# Revit family: Door-Exterior_Interior-Simpson-Sash-Three_Quarter_Glass-Single
name_source: partatom
category: Doors
revit_build: Autodesk Revit Architecture 2012 (Build: 20110916_2132(x64)
units: mm (PartAtom-declared; Revit-internal decimal feet)

## types (483) — shared parameters
Assembly Code = B2030230
Bottom Panel Height = 0' - 11 5/8"
Bottom Rail Height = 0' - 8 11/16"
Construction Type = Wood
Frame = Wood - Simpson Doors - Douglas Fir
Frame Projection Ext. = 0' - 1"
Frame Projection Int. = 0' - 1"
Frame Type = Frame : Standard
Frame Width = 0' - 3"
Function = Exterior
Glass = Glass - Simpson Doors - Clear
Glass Options = http://simpsondoor.com
Innerbond Double Hip-Raised Panel = Yes
Manufacturer = Simpson Door Company
Middle Rail Height = 0' - 6 1/2"
Muntin Width = 0' - 0 1/2"
Ovolo Construction = Yes
Panel = Wood - Simpson Doors - Douglas Fir
Panel Divider Width = 0' - 3 1/2"
Panel Stile Width = 0' - 5"
Product Documentation Link = http://www.simpsondoor.com
Product Page URL = http://www.simpsondoor.com
Thickness = 0' - 1 3/4"
Thickness Note = comes in 1 3/4" and 2 1/4" Thickness. Default is set to 1 3/4"
Top Rail Height = 0' - 3 15/16"
URL = http://www.simpsondoor.com
UltraBlock Note = This Door Comes with The Option of UltraBlock Technology. It is Turn On as a Default
UltraBlock Option = Yes
Wall Closure = By host
WaterBarrier Note = This Door Comes with The Option of WaterBarrier with UltraBlock Technology. It is Turn Off as a Default
WaterBarrier with UltraBlock Technology = No
Wood Species = http://simpsondoor.com
Wood Species Note = Available in Any Wood Species

## per-type parameters (varying)
| type | Description | Height | Model | Number of Horizontal Muntins | Number of Panel Dividers | Number of Vertical Muntins | Rough Height | Rough Width | Width |
| 501 Exterior Sash 30x80 Ovolo Raised Panel | Exterior Sash - Single Lite - Single Panel | 6' - 8" | 501 | 0 | 0 | 0 | 6' - 10" | 2' - 10" | 2' - 6" |
| 501 Exterior Sash 30x84 Ovolo Raised Panel | Exterior Sash - Single Lite - Single Panel | 7' - 0" | 501 | 0 | 0 | 0 | 7' - 2" | 2' - 10" | 2' - 6" |
| 501 Exterior Sash 30x96 Ovolo Raised Panel | Exterior Sash - Single Lite - Single Panel | 8' - 0" | 501 | 0 | 0 | 0 | 8' - 2" | 2' - 10" | 2' - 6" |
| 501 Exterior Sash 32x80 Ovolo Raised Panel | Exterior Sash - Single Lite - Single Panel | 6' - 8" | 501 | 0 | 0 | 0 | 6' - 10" | 3' - 0" | 2' - 8" |
| 501 Exterior Sash 32x84 Ovolo Raised Panel | Exterior Sash - Single Lite - Single Panel | 7' - 0" | 501 | 0 | 0 | 0 | 7' - 2" | 3' - 0" | 2' - 8" |
| 501 Exterior Sash 32x96 Ovolo Raised Panel | Exterior Sash - Single Lite - Single Panel | 8' - 0" | 501 | 0 | 0 | 0 | 8' - 2" | 3' - 0" | 2' - 8" |
| 501 Exterior Sash 34x80 Ovolo Raised Panel | Exterior Sash - Single Lite - Single Panel | 6' - 8" | 501 | 0 | 0 | 0 | 6' - 10" | 3' - 2" | 2' - 10" |
| 501 Exterior Sash 34x84 Ovolo Raised Panel | Exterior Sash - Single Lite - Single Panel | 7' - 0" | 501 | 0 | 0 | 0 | 7' - 2" | 3' - 2" | 2' - 10" |
| 501 Exterior Sash 34x96 Ovolo Raised Panel | Exterior Sash - Single Lite - Single Panel | 8' - 0" | 501 | 0 | 0 | 0 | 8' - 2" | 3' - 2" | 2' - 10" |
| 501 Exterior Sash 36x80 Ovolo Raised Panel | Exterior Sash - Single Lite - Single Panel | 6' - 8" | 501 | 0 | 0 | 0 | 6' - 10" | 3' - 4" | 3' - 0" |
| 501 Exterior Sash 36x84 Ovolo Raised Panel | Exterior Sash - Single Lite - Single Panel | 7' - 0" | 501 | 0 | 0 | 0 | 7' - 2" | 3' - 4" | 3' - 0" |
| 501 Exterior Sash 36x96 Ovolo Raised Panel | Exterior Sash - Single Lite - Single Panel | 8' - 0" | 501 | 0 | 0 | 0 | 8' - 2" | 3' - 4" | 3' - 0" |
| 501 Exterior Sash 38x80 Ovolo Raised Panel | Exterior Sash - Single Lite - Single Panel | 6' - 8" | 501 | 0 | 0 | 0 | 6' - 10" | 3' - 6" | 3' - 2" |
| 501 Exterior Sash 38x84 Ovolo Raised Panel | Exterior Sash - Single Lite - Single Panel | 7' - 0" | 501 | 0 | 0 | 0 | 7' - 2" | 3' - 6" | 3' - 2" |
| 501 Exterior Sash 38x96 Ovolo Raised Panel | Exterior Sash - Single Lite - Single Panel | 8' - 0" | 501 | 0 | 0 | 0 | 8' - 2" | 3' - 6" | 3' - 2" |
| 501 Exterior Sash 40x80 Ovolo Raised Panel | Exterior Sash - Single Lite - Single Panel | 6' - 8" | 501 | 0 | 0 | 0 | 6' - 10" | 3' - 8" | 3' - 4" |
| 501 Exterior Sash 40x84 Ovolo Raised Panel | Exterior Sash - Single Lite - Single Panel | 7' - 0" | 501 | 0 | 0 | 0 | 7' - 2" | 3' - 8" | 3' - 4" |
| 501 Exterior Sash 40x96 Ovolo Raised Panel | Exterior Sash - Single Lite - Single Panel | 8' - 0" | 501 | 0 | 0 | 0 | 8' - 2" | 3' - 8" | 3' - 4" |
| 501 Exterior Sash 42x80 Ovolo Raised Panel | Exterior Sash - Single Lite - Single Panel | 6' - 8" | 501 | 0 | 0 | 0 | 6' - 10" | 3' - 10" | 3' - 6" |
| 501 Exterior Sash 42x84 Ovolo Raised Panel | Exterior Sash - Single Lite - Single Panel | 7' - 0" | 501 | 0 | 0 | 0 | 7' - 2" | 3' - 10" | 3' - 6" |
| 501 Exterior Sash 42x96 Ovolo Raised Panel | Exterior Sash - Single Lite - Single Panel | 8' - 0" | 501 | 0 | 0 | 0 | 8' - 2" | 3' - 10" | 3' - 6" |
| 504 Exterior Sash 30x80 Ovolo Raised Panel | Exterior Sash - Four Lite - Single Panel | 6' - 8" | 504 | 1 | 0 | 1 | 6' - 10" | 2' - 10" | 2' - 6" |
| 504 Exterior Sash 30x84 Ovolo Raised Panel | Exterior Sash - Four Lite - Single Panel | 7' - 0" | 504 | 1 | 0 | 1 | 7' - 2" | 2' - 10" | 2' - 6" |
| 504 Exterior Sash 30x96 Ovolo Raised Panel | Exterior Sash - Four Lite - Single Panel | 8' - 0" | 504 | 1 | 0 | 1 | 8' - 2" | 2' - 10" | 2' - 6" |
| 504 Exterior Sash 32x80 Ovolo Raised Panel | Exterior Sash - Four Lite - Single Panel | 6' - 8" | 504 | 1 | 0 | 1 | 6' - 10" | 3' - 0" | 2' - 8" |
| 504 Exterior Sash 32x84 Ovolo Raised Panel | Exterior Sash - Four Lite - Single Panel | 7' - 0" | 504 | 1 | 0 | 1 | 7' - 2" | 3' - 0" | 2' - 8" |
| 504 Exterior Sash 32x96 Ovolo Raised Panel | Exterior Sash - Four Lite - Single Panel | 8' - 0" | 504 | 1 | 0 | 1 | 8' - 2" | 3' - 0" | 2' - 8" |
| 504 Exterior Sash 34x80 Ovolo Raised Panel | Exterior Sash - Four Lite - Single Panel | 6' - 8" | 504 | 1 | 0 | 1 | 6' - 10" | 3' - 2" | 2' - 10" |
| 504 Exterior Sash 34x84 Ovolo Raised Panel | Exterior Sash - Four Lite - Single Panel | 7' - 0" | 504 | 1 | 0 | 1 | 7' - 2" | 3' - 2" | 2' - 10" |
| 504 Exterior Sash 34x96 Ovolo Raised Panel | Exterior Sash - Four Lite - Single Panel | 8' - 0" | 504 | 1 | 0 | 1 | 8' - 2" | 3' - 2" | 2' - 10" |
| 504 Exterior Sash 36x80 Ovolo Raised Panel | Exterior Sash - Four Lite - Single Panel | 6' - 8" | 504 | 1 | 0 | 1 | 6' - 10" | 3' - 4" | 3' - 0" |
| 504 Exterior Sash 36x84 Ovolo Raised Panel | Exterior Sash - Four Lite - Single Panel | 7' - 0" | 504 | 1 | 0 | 1 | 7' - 2" | 3' - 4" | 3' - 0" |
| 504 Exterior Sash 36x96 Ovolo Raised Panel | Exterior Sash - Four Lite - Single Panel | 8' - 0" | 504 | 1 | 0 | 1 | 8' - 2" | 3' - 4" | 3' - 0" |
| 504 Exterior Sash 38x80 Ovolo Raised Panel | Exterior Sash - Four Lite - Single Panel | 6' - 8" | 504 | 1 | 0 | 1 | 6' - 10" | 3' - 6" | 3' - 2" |
| 504 Exterior Sash 38x84 Ovolo Raised Panel | Exterior Sash - Four Lite - Single Panel | 7' - 0" | 504 | 1 | 0 | 1 | 7' - 2" | 3' - 6" | 3' - 2" |
| 504 Exterior Sash 38x96 Ovolo Raised Panel | Exterior Sash - Four Lite - Single Panel | 8' - 0" | 504 | 1 | 0 | 1 | 8' - 2" | 3' - 6" | 3' - 2" |
| 504 Exterior Sash 40x80 Ovolo Raised Panel | Exterior Sash - Four Lite - Single Panel | 6' - 8" | 504 | 1 | 0 | 1 | 6' - 10" | 3' - 8" | 3' - 4" |
| 504 Exterior Sash 40x84 Ovolo Raised Panel | Exterior Sash - Four Lite - Single Panel | 7' - 0" | 504 | 1 | 0 | 1 | 7' - 2" | 3' - 8" | 3' - 4" |
| 504 Exterior Sash 40x96 Ovolo Raised Panel | Exterior Sash - Four Lite - Single Panel | 8' - 0" | 504 | 1 | 0 | 1 | 8' - 2" | 3' - 8" | 3' - 4" |
| 504 Exterior Sash 42x80 Ovolo Raised Panel | Exterior Sash - Four Lite - Single Panel | 6' - 8" | 504 | 1 | 0 | 1 | 6' - 10" | 3' - 10" | 3' - 6" |
| 504 Exterior Sash 42x84 Ovolo Raised Panel | Exterior Sash - Four Lite - Single Panel | 7' - 0" | 504 | 1 | 0 | 1 | 7' - 2" | 3' - 10" | 3' - 6" |
| 504 Exterior Sash 42x96 Ovolo Raised Panel | Exterior Sash - Four Lite - Single Panel | 8' - 0" | 504 | 1 | 0 | 1 | 8' - 2" | 3' - 10" | 3' - 6" |
| 506 Exterior Sash 30x80 Ovolo Raised Panel | Exterior Sash - Six Lite - Single Panel | 6' - 8" | 506 | 2 | 0 | 1 | 6' - 10" | 2' - 10" | 2' - 6" |
| 506 Exterior Sash 30x84 Ovolo Raised Panel | Exterior Sash - Six Lite - Single Panel | 7' - 0" | 506 | 2 | 0 | 1 | 7' - 2" | 2' - 10" | 2' - 6" |
| 506 Exterior Sash 30x96 Ovolo Raised Panel | Exterior Sash - Six Lite - Single Panel | 8' - 0" | 506 | 2 | 0 | 1 | 8' - 2" | 2' - 10" | 2' - 6" |
| 506 Exterior Sash 32x80 Ovolo Raised Panel | Exterior Sash - Six Lite - Single Panel | 6' - 8" | 506 | 2 | 0 | 1 | 6' - 10" | 3' - 0" | 2' - 8" |
| 506 Exterior Sash 32x84 Ovolo Raised Panel | Exterior Sash - Six Lite - Single Panel | 7' - 0" | 506 | 2 | 0 | 1 | 7' - 2" | 3' - 0" | 2' - 8" |
| 506 Exterior Sash 32x96 Ovolo Raised Panel | Exterior Sash - Six Lite - Single Panel | 8' - 0" | 506 | 2 | 0 | 1 | 8' - 2" | 3' - 0" | 2' - 8" |
| 506 Exterior Sash 34x80 Ovolo Raised Panel | Exterior Sash - Six Lite - Single Panel | 6' - 8" | 506 | 2 | 0 | 1 | 6' - 10" | 3' - 2" | 2' - 10" |
| 506 Exterior Sash 34x84 Ovolo Raised Panel | Exterior Sash - Six Lite - Single Panel | 7' - 0" | 506 | 2 | 0 | 1 | 7' - 2" | 3' - 2" | 2' - 10" |
| 506 Exterior Sash 34x96 Ovolo Raised Panel | Exterior Sash - Six Lite - Single Panel | 8' - 0" | 506 | 2 | 0 | 1 | 8' - 2" | 3' - 2" | 2' - 10" |
| 506 Exterior Sash 36x80 Ovolo Raised Panel | Exterior Sash - Six Lite - Single Panel | 6' - 8" | 506 | 2 | 0 | 1 | 6' - 10" | 3' - 4" | 3' - 0" |
| 506 Exterior Sash 36x84 Ovolo Raised Panel | Exterior Sash - Six Lite - Single Panel | 7' - 0" | 506 | 2 | 0 | 1 | 7' - 2" | 3' - 4" | 3' - 0" |
| 506 Exterior Sash 36x96 Ovolo Raised Panel | Exterior Sash - Six Lite - Single Panel | 8' - 0" | 506 | 2 | 0 | 1 | 8' - 2" | 3' - 4" | 3' - 0" |
| 506 Exterior Sash 38x80 Ovolo Raised Panel | Exterior Sash - Six Lite - Single Panel | 6' - 8" | 506 | 2 | 0 | 1 | 6' - 10" | 3' - 6" | 3' - 2" |
| 506 Exterior Sash 38x84 Ovolo Raised Panel | Exterior Sash - Six Lite - Single Panel | 7' - 0" | 506 | 2 | 0 | 1 | 7' - 2" | 3' - 6" | 3' - 2" |
| 506 Exterior Sash 38x96 Ovolo Raised Panel | Exterior Sash - Six Lite - Single Panel | 8' - 0" | 506 | 2 | 0 | 1 | 8' - 2" | 3' - 6" | 3' - 2" |
| 506 Exterior Sash 40x80 Ovolo Raised Panel | Exterior Sash - Six Lite - Single Panel | 6' - 8" | 506 | 2 | 0 | 1 | 6' - 10" | 3' - 8" | 3' - 4" |
| 506 Exterior Sash 40x84 Ovolo Raised Panel | Exterior Sash - Six Lite - Single Panel | 7' - 0" | 506 | 2 | 0 | 1 | 7' - 2" | 3' - 8" | 3' - 4" |
| 506 Exterior Sash 40x96 Ovolo Raised Panel | Exterior Sash - Six Lite - Single Panel | 8' - 0" | 506 | 2 | 0 | 1 | 8' - 2" | 3' - 8" | 3' - 4" |
| 506 Exterior Sash 42x80 Ovolo Raised Panel | Exterior Sash - Six Lite - Single Panel | 6' - 8" | 506 | 2 | 0 | 1 | 6' - 10" | 3' - 10" | 3' - 6" |
| 506 Exterior Sash 42x84 Ovolo Raised Panel | Exterior Sash - Six Lite - Single Panel | 7' - 0" | 506 | 2 | 0 | 1 | 7' - 2" | 3' - 10" | 3' - 6" |
| 506 Exterior Sash 42x96 Ovolo Raised Panel | Exterior Sash - Six Lite - Single Panel | 8' - 0" | 506 | 2 | 0 | 1 | 8' - 2" | 3' - 10" | 3' - 6" |
| 508 Exterior Sash 30x80 Ovolo Raised Panel | Exterior Sash - Eight Lite - Single Panel | 6' - 8" | 508 | 3 | 0 | 1 | 6' - 10" | 2' - 10" | 2' - 6" |
| 508 Exterior Sash 30x84 Ovolo Raised Panel | Exterior Sash - Eight Lite - Single Panel | 7' - 0" | 508 | 3 | 0 | 1 | 7' - 2" | 2' - 10" | 2' - 6" |
| 508 Exterior Sash 30x96 Ovolo Raised Panel | Exterior Sash - Eight Lite - Single Panel | 8' - 0" | 508 | 3 | 0 | 1 | 8' - 2" | 2' - 10" | 2' - 6" |
| 508 Exterior Sash 32x80 Ovolo Raised Panel | Exterior Sash - Eight Lite - Single Panel | 6' - 8" | 508 | 3 | 0 | 1 | 6' - 10" | 3' - 0" | 2' - 8" |
| 508 Exterior Sash 32x84 Ovolo Raised Panel | Exterior Sash - Eight Lite - Single Panel | 7' - 0" | 508 | 3 | 0 | 1 | 7' - 2" | 3' - 0" | 2' - 8" |
| 508 Exterior Sash 32x96 Ovolo Raised Panel | Exterior Sash - Eight Lite - Single Panel | 8' - 0" | 508 | 3 | 0 | 1 | 8' - 2" | 3' - 0" | 2' - 8" |
| 508 Exterior Sash 34x80 Ovolo Raised Panel | Exterior Sash - Eight Lite - Single Panel | 6' - 8" | 508 | 3 | 0 | 1 | 6' - 10" | 3' - 2" | 2' - 10" |
| 508 Exterior Sash 34x84 Ovolo Raised Panel | Exterior Sash - Eight Lite - Single Panel | 7' - 0" | 508 | 3 | 0 | 1 | 7' - 2" | 3' - 2" | 2' - 10" |
| 508 Exterior Sash 34x96 Ovolo Raised Panel | Exterior Sash - Eight Lite - Single Panel | 8' - 0" | 508 | 3 | 0 | 1 | 8' - 2" | 3' - 2" | 2' - 10" |
| 508 Exterior Sash 36x80 Ovolo Raised Panel | Exterior Sash - Eight Lite - Single Panel | 6' - 8" | 508 | 3 | 0 | 1 | 6' - 10" | 3' - 4" | 3' - 0" |
| 508 Exterior Sash 36x84 Ovolo Raised Panel | Exterior Sash - Eight Lite - Single Panel | 7' - 0" | 508 | 3 | 0 | 1 | 7' - 2" | 3' - 4" | 3' - 0" |
| 508 Exterior Sash 36x96 Ovolo Raised Panel | Exterior Sash - Eight Lite - Single Panel | 8' - 0" | 508 | 3 | 0 | 1 | 8' - 2" | 3' - 4" | 3' - 0" |
| 508 Exterior Sash 38x80 Ovolo Raised Panel | Exterior Sash - Eight Lite - Single Panel | 6' - 8" | 508 | 3 | 0 | 1 | 6' - 10" | 3' - 6" | 3' - 2" |
| 508 Exterior Sash 38x84 Ovolo Raised Panel | Exterior Sash - Eight Lite - Single Panel | 7' - 0" | 508 | 3 | 0 | 1 | 7' - 2" | 3' - 6" | 3' - 2" |
| 508 Exterior Sash 38x96 Ovolo Raised Panel | Exterior Sash - Eight Lite - Single Panel | 8' - 0" | 508 | 3 | 0 | 1 | 8' - 2" | 3' - 6" | 3' - 2" |
| 508 Exterior Sash 40x80 Ovolo Raised Panel | Exterior Sash - Eight Lite - Single Panel | 6' - 8" | 508 | 3 | 0 | 1 | 6' - 10" | 3' - 8" | 3' - 4" |
| 508 Exterior Sash 40x84 Ovolo Raised Panel | Exterior Sash - Eight Lite - Single Panel | 7' - 0" | 508 | 3 | 0 | 1 | 7' - 2" | 3' - 8" | 3' - 4" |
| 508 Exterior Sash 40x96 Ovolo Raised Panel | Exterior Sash - Eight Lite - Single Panel | 8' - 0" | 508 | 3 | 0 | 1 | 8' - 2" | 3' - 8" | 3' - 4" |
| 508 Exterior Sash 42x80 Ovolo Raised Panel | Exterior Sash - Eight Lite - Single Panel | 6' - 8" | 508 | 3 | 0 | 1 | 6' - 10" | 3' - 10" | 3' - 6" |
| 508 Exterior Sash 42x84 Ovolo Raised Panel | Exterior Sash - Eight Lite - Single Panel | 7' - 0" | 508 | 3 | 0 | 1 | 7' - 2" | 3' - 10" | 3' - 6" |
| 508 Exterior Sash 42x96 Ovolo Raised Panel | Exterior Sash - Eight Lite - Single Panel | 8' - 0" | 508 | 3 | 0 | 1 | 8' - 2" | 3' - 10" | 3' - 6" |
| 512 Exterior Sash 30x80 Ovolo Raised Panel | Exterior Sash - Twelve Lite - Single Panel | 6' - 8" | 512 | 3 | 0 | 2 | 6' - 10" | 2' - 10" | 2' - 6" |
| 512 Exterior Sash 30x84 Ovolo Raised Panel | Exterior Sash - Twelve Lite - Single Panel | 7' - 0" | 512 | 3 | 0 | 2 | 7' - 2" | 2' - 10" | 2' - 6" |
| 512 Exterior Sash 30x96 Ovolo Raised Panel | Exterior Sash - Twelve Lite - Single Panel | 8' - 0" | 512 | 3 | 0 | 2 | 8' - 2" | 2' - 10" | 2' - 6" |
| 512 Exterior Sash 32x80 Ovolo Raised Panel | Exterior Sash - Twelve Lite - Single Panel | 6' - 8" | 512 | 3 | 0 | 2 | 6' - 10" | 3' - 0" | 2' - 8" |
| 512 Exterior Sash 32x84 Ovolo Raised Panel | Exterior Sash - Twelve Lite - Single Panel | 7' - 0" | 512 | 3 | 0 | 2 | 7' - 2" | 3' - 0" | 2' - 8" |
| 512 Exterior Sash 32x96 Ovolo Raised Panel | Exterior Sash - Twelve Lite - Single Panel | 8' - 0" | 512 | 3 | 0 | 2 | 8' - 2" | 3' - 0" | 2' - 8" |
| 512 Exterior Sash 34x80 Ovolo Raised Panel | Exterior Sash - Twelve Lite - Single Panel | 6' - 8" | 512 | 3 | 0 | 2 | 6' - 10" | 3' - 2" | 2' - 10" |
| 512 Exterior Sash 34x84 Ovolo Raised Panel | Exterior Sash - Twelve Lite - Single Panel | 7' - 0" | 512 | 3 | 0 | 2 | 7' - 2" | 3' - 2" | 2' - 10" |
| 512 Exterior Sash 34x96 Ovolo Raised Panel | Exterior Sash - Twelve Lite - Single Panel | 8' - 0" | 512 | 3 | 0 | 2 | 8' - 2" | 3' - 2" | 2' - 10" |
| 512 Exterior Sash 36x80 Ovolo Raised Panel | Exterior Sash - Twelve Lite - Single Panel | 6' - 8" | 512 | 3 | 0 | 2 | 6' - 10" | 3' - 4" | 3' - 0" |
| 512 Exterior Sash 36x84 Ovolo Raised Panel | Exterior Sash - Twelve Lite - Single Panel | 7' - 0" | 512 | 3 | 0 | 2 | 7' - 2" | 3' - 4" | 3' - 0" |
| 512 Exterior Sash 36x96 Ovolo Raised Panel | Exterior Sash - Twelve Lite - Single Panel | 8' - 0" | 512 | 3 | 0 | 2 | 8' - 2" | 3' - 4" | 3' - 0" |
| 512 Exterior Sash 38x80 Ovolo Raised Panel | Exterior Sash - Twelve Lite - Single Panel | 6' - 8" | 512 | 3 | 0 | 2 | 6' - 10" | 3' - 6" | 3' - 2" |
| 512 Exterior Sash 38x84 Ovolo Raised Panel | Exterior Sash - Twelve Lite - Single Panel | 7' - 0" | 512 | 3 | 0 | 2 | 7' - 2" | 3' - 6" | 3' - 2" |
| 512 Exterior Sash 38x96 Ovolo Raised Panel | Exterior Sash - Twelve Lite - Single Panel | 8' - 0" | 512 | 3 | 0 | 2 | 8' - 2" | 3' - 6" | 3' - 2" |
| 512 Exterior Sash 40x80 Ovolo Raised Panel | Exterior Sash - Twelve Lite - Single Panel | 6' - 8" | 512 | 3 | 0 | 2 | 6' - 10" | 3' - 8" | 3' - 4" |
| 512 Exterior Sash 40x84 Ovolo Raised Panel | Exterior Sash - Twelve Lite - Single Panel | 7' - 0" | 512 | 3 | 0 | 2 | 7' - 2" | 3' - 8" | 3' - 4" |
| 512 Exterior Sash 40x96 Ovolo Raised Panel | Exterior Sash - Twelve Lite - Single Panel | 8' - 0" | 512 | 3 | 0 | 2 | 8' - 2" | 3' - 8" | 3' - 4" |
| 512 Exterior Sash 42x80 Ovolo Raised Panel | Exterior Sash - Twelve Lite - Single Panel | 6' - 8" | 512 | 3 | 0 | 2 | 6' - 10" | 3' - 10" | 3' - 6" |
| 512 Exterior Sash 42x84 Ovolo Raised Panel | Exterior Sash - Twelve Lite - Single Panel | 7' - 0" | 512 | 3 | 0 | 2 | 7' - 2" | 3' - 10" | 3' - 6" |
| 512 Exterior Sash 42x96 Ovolo Raised Panel | Exterior Sash - Twelve Lite - Single Panel | 8' - 0" | 512 | 3 | 0 | 2 | 8' - 2" | 3' - 10" | 3' - 6" |
| 7501 Thermal French & Sash 30x80 Ovolo Raised Panel | Thermal Sash TDL - Single Lite - Single Panel | 6' - 8" | 7501 | 0 | 0 | 0 | 6' - 10" | 2' - 10" | 2' - 6" |
| 7501 Thermal French & Sash 30x84 Ovolo Raised Panel | Thermal Sash TDL - Single Lite - Single Panel | 7' - 0" | 7501 | 0 | 0 | 0 | 7' - 2" | 2' - 10" | 2' - 6" |
| 7501 Thermal French & Sash 30x96 Ovolo Raised Panel | Thermal Sash TDL - Single Lite - Single Panel | 8' - 0" | 7501 | 0 | 0 | 0 | 8' - 2" | 2' - 10" | 2' - 6" |
| 7501 Thermal French & Sash 32x80 Ovolo Raised Panel | Thermal Sash TDL - Single Lite - Single Panel | 6' - 8" | 7501 | 0 | 0 | 0 | 6' - 10" | 3' - 0" | 2' - 8" |
| 7501 Thermal French & Sash 32x84 Ovolo Raised Panel | Thermal Sash TDL - Single Lite - Single Panel | 7' - 0" | 7501 | 0 | 0 | 0 | 7' - 2" | 3' - 0" | 2' - 8" |
| 7501 Thermal French & Sash 32x96 Ovolo Raised Panel | Thermal Sash TDL - Single Lite - Single Panel | 8' - 0" | 7501 | 0 | 0 | 0 | 8' - 2" | 3' - 0" | 2' - 8" |
| 7501 Thermal French & Sash 34x80 Ovolo Raised Panel | Thermal Sash TDL - Single Lite - Single Panel | 6' - 8" | 7501 | 0 | 0 | 0 | 6' - 10" | 3' - 2" | 2' - 10" |
| 7501 Thermal French & Sash 34x84 Ovolo Raised Panel | Thermal Sash TDL - Single Lite - Single Panel | 7' - 0" | 7501 | 0 | 0 | 0 | 7' - 2" | 3' - 2" | 2' - 10" |
| 7501 Thermal French & Sash 34x96 Ovolo Raised Panel | Thermal Sash TDL - Single Lite - Single Panel | 8' - 0" | 7501 | 0 | 0 | 0 | 8' - 2" | 3' - 2" | 2' - 10" |
| 7501 Thermal French & Sash 36x80 Ovolo Raised Panel | Thermal Sash TDL - Single Lite - Single Panel | 6' - 8" | 7501 | 0 | 0 | 0 | 6' - 10" | 3' - 4" | 3' - 0" |
| 7501 Thermal French & Sash 36x84 Ovolo Raised Panel | Thermal Sash TDL - Single Lite - Single Panel | 7' - 0" | 7501 | 0 | 0 | 0 | 7' - 2" | 3' - 4" | 3' - 0" |
| 7501 Thermal French & Sash 36x96 Ovolo Raised Panel | Thermal Sash TDL - Single Lite - Single Panel | 8' - 0" | 7501 | 0 | 0 | 0 | 8' - 2" | 3' - 4" | 3' - 0" |
| 7501 Thermal French & Sash 38x80 Ovolo Raised Panel | Thermal Sash TDL - Single Lite - Single Panel | 6' - 8" | 7501 | 0 | 0 | 0 | 6' - 10" | 3' - 6" | 3' - 2" |
| 7501 Thermal French & Sash 38x84 Ovolo Raised Panel | Thermal Sash TDL - Single Lite - Single Panel | 7' - 0" | 7501 | 0 | 0 | 0 | 7' - 2" | 3' - 6" | 3' - 2" |
| 7501 Thermal French & Sash 38x96 Ovolo Raised Panel | Thermal Sash TDL - Single Lite - Single Panel | 8' - 0" | 7501 | 0 | 0 | 0 | 8' - 2" | 3' - 6" | 3' - 2" |
| 7501 Thermal French & Sash 40x80 Ovolo Raised Panel | Thermal Sash TDL - Single Lite - Single Panel | 6' - 8" | 7501 | 0 | 0 | 0 | 6' - 10" | 3' - 8" | 3' - 4" |
| 7501 Thermal French & Sash 40x84 Ovolo Raised Panel | Thermal Sash TDL - Single Lite - Single Panel | 7' - 0" | 7501 | 0 | 0 | 0 | 7' - 2" | 3' - 8" | 3' - 4" |
| 7501 Thermal French & Sash 40x96 Ovolo Raised Panel | Thermal Sash TDL - Single Lite - Single Panel | 8' - 0" | 7501 | 0 | 0 | 0 | 8' - 2" | 3' - 8" | 3' - 4" |
| 7501 Thermal French & Sash 42x80 Ovolo Raised Panel | Thermal Sash TDL - Single Lite - Single Panel | 6' - 8" | 7501 | 0 | 0 | 0 | 6' - 10" | 3' - 10" | 3' - 6" |
| 7501 Thermal French & Sash 42x84 Ovolo Raised Panel | Thermal Sash TDL - Single Lite - Single Panel | 7' - 0" | 7501 | 0 | 0 | 0 | 7' - 2" | 3' - 10" | 3' - 6" |
| 7501 Thermal French & Sash 42x96 Ovolo Raised Panel | Thermal Sash TDL - Single Lite - Single Panel | 8' - 0" | 7501 | 0 | 0 | 0 | 8' - 2" | 3' - 10" | 3' - 6" |
| 7504 Thermal French & Sash 30x80 Ovolo Raised Panel | Thermal Sash TDL - Four Lite - Single Panel | 6' - 8" | 7504 | 1 | 0 | 1 | 6' - 10" | 2' - 10" | 2' - 6" |
| 7504 Thermal French & Sash 30x84 Ovolo Raised Panel | Thermal Sash TDL - Four Lite - Single Panel | 7' - 0" | 7504 | 1 | 0 | 1 | 7' - 2" | 2' - 10" | 2' - 6" |
| 7504 Thermal French & Sash 30x96 Ovolo Raised Panel | Thermal Sash TDL - Four Lite - Single Panel | 8' - 0" | 7504 | 1 | 0 | 1 | 8' - 2" | 2' - 10" | 2' - 6" |
| 7504 Thermal French & Sash 32x80 Ovolo Raised Panel | Thermal Sash TDL - Four Lite - Single Panel | 6' - 8" | 7504 | 1 | 0 | 1 | 6' - 10" | 3' - 0" | 2' - 8" |
| 7504 Thermal French & Sash 32x84 Ovolo Raised Panel | Thermal Sash TDL - Four Lite - Single Panel | 7' - 0" | 7504 | 1 | 0 | 1 | 7' - 2" | 3' - 0" | 2' - 8" |
| 7504 Thermal French & Sash 32x96 Ovolo Raised Panel | Thermal Sash TDL - Four Lite - Single Panel | 8' - 0" | 7504 | 1 | 0 | 1 | 8' - 2" | 3' - 0" | 2' - 8" |
| 7504 Thermal French & Sash 34x80 Ovolo Raised Panel | Thermal Sash TDL - Four Lite - Single Panel | 6' - 8" | 7504 | 1 | 0 | 1 | 6' - 10" | 3' - 2" | 2' - 10" |
| 7504 Thermal French & Sash 34x84 Ovolo Raised Panel | Thermal Sash TDL - Four Lite - Single Panel | 7' - 0" | 7504 | 1 | 0 | 1 | 7' - 2" | 3' - 2" | 2' - 10" |
| 7504 Thermal French & Sash 34x96 Ovolo Raised Panel | Thermal Sash TDL - Four Lite - Single Panel | 8' - 0" | 7504 | 1 | 0 | 1 | 8' - 2" | 3' - 2" | 2' - 10" |
| 7504 Thermal French & Sash 36x80 Ovolo Raised Panel | Thermal Sash TDL - Four Lite - Single Panel | 6' - 8" | 7504 | 1 | 0 | 1 | 6' - 10" | 3' - 4" | 3' - 0" |
| 7504 Thermal French & Sash 36x84 Ovolo Raised Panel | Thermal Sash TDL - Four Lite - Single Panel | 7' - 0" | 7504 | 1 | 0 | 1 | 7' - 2" | 3' - 4" | 3' - 0" |
| 7504 Thermal French & Sash 36x96 Ovolo Raised Panel | Thermal Sash TDL - Four Lite - Single Panel | 8' - 0" | 7504 | 1 | 0 | 1 | 8' - 2" | 3' - 4" | 3' - 0" |
| 7504 Thermal French & Sash 38x80 Ovolo Raised Panel | Thermal Sash TDL - Four Lite - Single Panel | 6' - 8" | 7504 | 1 | 0 | 1 | 6' - 10" | 3' - 6" | 3' - 2" |
| 7504 Thermal French & Sash 38x84 Ovolo Raised Panel | Thermal Sash TDL - Four Lite - Single Panel | 7' - 0" | 7504 | 1 | 0 | 1 | 7' - 2" | 3' - 6" | 3' - 2" |
| 7504 Thermal French & Sash 38x96 Ovolo Raised Panel | Thermal Sash TDL - Four Lite - Single Panel | 8' - 0" | 7504 | 1 | 0 | 1 | 8' - 2" | 3' - 6" | 3' - 2" |
| 7504 Thermal French & Sash 40x80 Ovolo Raised Panel | Thermal Sash TDL - Four Lite - Single Panel | 6' - 8" | 7504 | 1 | 0 | 1 | 6' - 10" | 3' - 8" | 3' - 4" |
| 7504 Thermal French & Sash 40x84 Ovolo Raised Panel | Thermal Sash TDL - Four Lite - Single Panel | 7' - 0" | 7504 | 1 | 0 | 1 | 7' - 2" | 3' - 8" | 3' - 4" |
| 7504 Thermal French & Sash 40x96 Ovolo Raised Panel | Thermal Sash TDL - Four Lite - Single Panel | 8' - 0" | 7504 | 1 | 0 | 1 | 8' - 2" | 3' - 8" | 3' - 4" |
| 7504 Thermal French & Sash 42x80 Ovolo Raised Panel | Thermal Sash TDL - Four Lite - Single Panel | 6' - 8" | 7504 | 1 | 0 | 1 | 6' - 10" | 3' - 10" | 3' - 6" |
| 7504 Thermal French & Sash 42x84 Ovolo Raised Panel | Thermal Sash TDL - Four Lite - Single Panel | 7' - 0" | 7504 | 1 | 0 | 1 | 7' - 2" | 3' - 10" | 3' - 6" |
| 7504 Thermal French & Sash 42x96 Ovolo Raised Panel | Thermal Sash TDL - Four Lite - Single Panel | 8' - 0" | 7504 | 1 | 0 | 1 | 8' - 2" | 3' - 10" | 3' - 6" |
| 7506 Thermal French & Sash 30x80 Ovolo Raised Panel | Thermal Sash TDL - Six Lite - Single Panel | 6' - 8" | 7506 | 2 | 0 | 1 | 6' - 10" | 2' - 10" | 2' - 6" |
| 7506 Thermal French & Sash 30x84 Ovolo Raised Panel | Thermal Sash TDL - Six Lite - Single Panel | 7' - 0" | 7506 | 2 | 0 | 1 | 7' - 2" | 2' - 10" | 2' - 6" |
| 7506 Thermal French & Sash 30x96 Ovolo Raised Panel | Thermal Sash TDL - Six Lite - Single Panel | 8' - 0" | 7506 | 2 | 0 | 1 | 8' - 2" | 2' - 10" | 2' - 6" |
| 7506 Thermal French & Sash 32x80 Ovolo Raised Panel | Thermal Sash TDL - Six Lite - Single Panel | 6' - 8" | 7506 | 2 | 0 | 1 | 6' - 10" | 3' - 0" | 2' - 8" |
| 7506 Thermal French & Sash 32x84 Ovolo Raised Panel | Thermal Sash TDL - Six Lite - Single Panel | 7' - 0" | 7506 | 2 | 0 | 1 | 7' - 2" | 3' - 0" | 2' - 8" |
| 7506 Thermal French & Sash 32x96 Ovolo Raised Panel | Thermal Sash TDL - Six Lite - Single Panel | 8' - 0" | 7506 | 2 | 0 | 1 | 8' - 2" | 3' - 0" | 2' - 8" |
| 7506 Thermal French & Sash 34x80 Ovolo Raised Panel | Thermal Sash TDL - Six Lite - Single Panel | 6' - 8" | 7506 | 2 | 0 | 1 | 6' - 10" | 3' - 2" | 2' - 10" |
| 7506 Thermal French & Sash 34x84 Ovolo Raised Panel | Thermal Sash TDL - Six Lite - Single Panel | 7' - 0" | 7506 | 2 | 0 | 1 | 7' - 2" | 3' - 2" | 2' - 10" |
| 7506 Thermal French & Sash 34x96 Ovolo Raised Panel | Thermal Sash TDL - Six Lite - Single Panel | 8' - 0" | 7506 | 2 | 0 | 1 | 8' - 2" | 3' - 2" | 2' - 10" |
| 7506 Thermal French & Sash 36x80 Ovolo Raised Panel | Thermal Sash TDL - Six Lite - Single Panel | 6' - 8" | 7506 | 2 | 0 | 1 | 6' - 10" | 3' - 4" | 3' - 0" |
| 7506 Thermal French & Sash 36x84 Ovolo Raised Panel | Thermal Sash TDL - Six Lite - Single Panel | 7' - 0" | 7506 | 2 | 0 | 1 | 7' - 2" | 3' - 4" | 3' - 0" |
| 7506 Thermal French & Sash 36x96 Ovolo Raised Panel | Thermal Sash TDL - Six Lite - Single Panel | 8' - 0" | 7506 | 2 | 0 | 1 | 8' - 2" | 3' - 4" | 3' - 0" |
| 7506 Thermal French & Sash 38x80 Ovolo Raised Panel | Thermal Sash TDL - Six Lite - Single Panel | 6' - 8" | 7506 | 2 | 0 | 1 | 6' - 10" | 3' - 6" | 3' - 2" |
| 7506 Thermal French & Sash 38x84 Ovolo Raised Panel | Thermal Sash TDL - Six Lite - Single Panel | 7' - 0" | 7506 | 2 | 0 | 1 | 7' - 2" | 3' - 6" | 3' - 2" |
| 7506 Thermal French & Sash 38x96 Ovolo Raised Panel | Thermal Sash TDL - Six Lite - Single Panel | 8' - 0" | 7506 | 2 | 0 | 1 | 8' - 2" | 3' - 6" | 3' - 2" |
| 7506 Thermal French & Sash 40x80 Ovolo Raised Panel | Thermal Sash TDL - Six Lite - Single Panel | 6' - 8" | 7506 | 2 | 0 | 1 | 6' - 10" | 3' - 8" | 3' - 4" |
| 7506 Thermal French & Sash 40x84 Ovolo Raised Panel | Thermal Sash TDL - Six Lite - Single Panel | 7' - 0" | 7506 | 2 | 0 | 1 | 7' - 2" | 3' - 8" | 3' - 4" |
| 7506 Thermal French & Sash 40x96 Ovolo Raised Panel | Thermal Sash TDL - Six Lite - Single Panel | 8' - 0" | 7506 | 2 | 0 | 1 | 8' - 2" | 3' - 8" | 3' - 4" |
| 7506 Thermal French & Sash 42x80 Ovolo Raised Panel | Thermal Sash TDL - Six Lite - Single Panel | 6' - 8" | 7506 | 2 | 0 | 1 | 6' - 10" | 3' - 10" | 3' - 6" |
| 7506 Thermal French & Sash 42x84 Ovolo Raised Panel | Thermal Sash TDL - Six Lite - Single Panel | 7' - 0" | 7506 | 2 | 0 | 1 | 7' - 2" | 3' - 10" | 3' - 6" |
| 7506 Thermal French & Sash 42x96 Ovolo Raised Panel | Thermal Sash TDL - Six Lite - Single Panel | 8' - 0" | 7506 | 2 | 0 | 1 | 8' - 2" | 3' - 10" | 3' - 6" |
| 7508 Thermal French & Sash 30x80 Ovolo Raised Panel | Thermal Sash TDL - Eight Lite - Single Panel | 6' - 8" | 7508 | 3 | 0 | 1 | 6' - 10" | 2' - 10" | 2' - 6" |
| 7508 Thermal French & Sash 30x84 Ovolo Raised Panel | Thermal Sash TDL - Eight Lite - Single Panel | 7' - 0" | 7508 | 3 | 0 | 1 | 7' - 2" | 2' - 10" | 2' - 6" |
| 7508 Thermal French & Sash 30x96 Ovolo Raised Panel | Thermal Sash TDL - Eight Lite - Single Panel | 8' - 0" | 7508 | 3 | 0 | 1 | 8' - 2" | 2' - 10" | 2' - 6" |
| 7508 Thermal French & Sash 32x80 Ovolo Raised Panel | Thermal Sash TDL - Eight Lite - Single Panel | 6' - 8" | 7508 | 3 | 0 | 1 | 6' - 10" | 3' - 0" | 2' - 8" |
| 7508 Thermal French & Sash 32x84 Ovolo Raised Panel | Thermal Sash TDL - Eight Lite - Single Panel | 7' - 0" | 7508 | 3 | 0 | 1 | 7' - 2" | 3' - 0" | 2' - 8" |
| 7508 Thermal French & Sash 32x96 Ovolo Raised Panel | Thermal Sash TDL - Eight Lite - Single Panel | 8' - 0" | 7508 | 3 | 0 | 1 | 8' - 2" | 3' - 0" | 2' - 8" |
| 7508 Thermal French & Sash 34x80 Ovolo Raised Panel | Thermal Sash TDL - Eight Lite - Single Panel | 6' - 8" | 7508 | 3 | 0 | 1 | 6' - 10" | 3' - 2" | 2' - 10" |
| 7508 Thermal French & Sash 34x84 Ovolo Raised Panel | Thermal Sash TDL - Eight Lite - Single Panel | 7' - 0" | 7508 | 3 | 0 | 1 | 7' - 2" | 3' - 2" | 2' - 10" |
| 7508 Thermal French & Sash 34x96 Ovolo Raised Panel | Thermal Sash TDL - Eight Lite - Single Panel | 8' - 0" | 7508 | 3 | 0 | 1 | 8' - 2" | 3' - 2" | 2' - 10" |
| 7508 Thermal French & Sash 36x80 Ovolo Raised Panel | Thermal Sash TDL - Eight Lite - Single Panel | 6' - 8" | 7508 | 3 | 0 | 1 | 6' - 10" | 3' - 4" | 3' - 0" |
| 7508 Thermal French & Sash 36x84 Ovolo Raised Panel | Thermal Sash TDL - Eight Lite - Single Panel | 7' - 0" | 7508 | 3 | 0 | 1 | 7' - 2" | 3' - 4" | 3' - 0" |
| 7508 Thermal French & Sash 36x96 Ovolo Raised Panel | Thermal Sash TDL - Eight Lite - Single Panel | 8' - 0" | 7508 | 3 | 0 | 1 | 8' - 2" | 3' - 4" | 3' - 0" |
| 7508 Thermal French & Sash 38x80 Ovolo Raised Panel | Thermal Sash TDL - Eight Lite - Single Panel | 6' - 8" | 7508 | 3 | 0 | 1 | 6' - 10" | 3' - 6" | 3' - 2" |
| 7508 Thermal French & Sash 38x84 Ovolo Raised Panel | Thermal Sash TDL - Eight Lite - Single Panel | 7' - 0" | 7508 | 3 | 0 | 1 | 7' - 2" | 3' - 6" | 3' - 2" |
| 7508 Thermal French & Sash 38x96 Ovolo Raised Panel | Thermal Sash TDL - Eight Lite - Single Panel | 8' - 0" | 7508 | 3 | 0 | 1 | 8' - 2" | 3' - 6" | 3' - 2" |
| 7508 Thermal French & Sash 40x80 Ovolo Raised Panel | Thermal Sash TDL - Eight Lite - Single Panel | 6' - 8" | 7508 | 3 | 0 | 1 | 6' - 10" | 3' - 8" | 3' - 4" |
| 7508 Thermal French & Sash 40x84 Ovolo Raised Panel | Thermal Sash TDL - Eight Lite - Single Panel | 7' - 0" | 7508 | 3 | 0 | 1 | 7' - 2" | 3' - 8" | 3' - 4" |
| 7508 Thermal French & Sash 40x96 Ovolo Raised Panel | Thermal Sash TDL - Eight Lite - Single Panel | 8' - 0" | 7508 | 3 | 0 | 1 | 8' - 2" | 3' - 8" | 3' - 4" |
| 7508 Thermal French & Sash 42x80 Ovolo Raised Panel | Thermal Sash TDL - Eight Lite - Single Panel | 6' - 8" | 7508 | 3 | 0 | 1 | 6' - 10" | 3' - 10" | 3' - 6" |
| 7508 Thermal French & Sash 42x84 Ovolo Raised Panel | Thermal Sash TDL - Eight Lite - Single Panel | 7' - 0" | 7508 | 3 | 0 | 1 | 7' - 2" | 3' - 10" | 3' - 6" |
| 7508 Thermal French & Sash 42x96 Ovolo Raised Panel | Thermal Sash TDL - Eight Lite - Single Panel | 8' - 0" | 7508 | 3 | 0 | 1 | 8' - 2" | 3' - 10" | 3' - 6" |
| 7512 Thermal French & Sash 30x80 Ovolo Raised Panel | Thermal Sash TDL - Twelve Lite - Single Panel | 6' - 8" | 7512 | 3 | 0 | 2 | 6' - 10" | 2' - 10" | 2' - 6" |
| 7512 Thermal French & Sash 30x84 Ovolo Raised Panel | Thermal Sash TDL - Twelve Lite - Single Panel | 7' - 0" | 7512 | 3 | 0 | 2 | 7' - 2" | 2' - 10" | 2' - 6" |
| 7512 Thermal French & Sash 30x96 Ovolo Raised Panel | Thermal Sash TDL - Twelve Lite - Single Panel | 8' - 0" | 7512 | 3 | 0 | 2 | 8' - 2" | 2' - 10" | 2' - 6" |
| 7512 Thermal French & Sash 32x80 Ovolo Raised Panel | Thermal Sash TDL - Twelve Lite - Single Panel | 6' - 8" | 7512 | 3 | 0 | 2 | 6' - 10" | 3' - 0" | 2' - 8" |
| 7512 Thermal French & Sash 32x84 Ovolo Raised Panel | Thermal Sash TDL - Twelve Lite - Single Panel | 7' - 0" | 7512 | 3 | 0 | 2 | 7' - 2" | 3' - 0" | 2' - 8" |
| 7512 Thermal French & Sash 32x96 Ovolo Raised Panel | Thermal Sash TDL - Twelve Lite - Single Panel | 8' - 0" | 7512 | 3 | 0 | 2 | 8' - 2" | 3' - 0" | 2' - 8" |
| 7512 Thermal French & Sash 34x80 Ovolo Raised Panel | Thermal Sash TDL - Twelve Lite - Single Panel | 6' - 8" | 7512 | 3 | 0 | 2 | 6' - 10" | 3' - 2" | 2' - 10" |
| 7512 Thermal French & Sash 34x84 Ovolo Raised Panel | Thermal Sash TDL - Twelve Lite - Single Panel | 7' - 0" | 7512 | 3 | 0 | 2 | 7' - 2" | 3' - 2" | 2' - 10" |
| 7512 Thermal French & Sash 34x96 Ovolo Raised Panel | Thermal Sash TDL - Twelve Lite - Single Panel | 8' - 0" | 7512 | 3 | 0 | 2 | 8' - 2" | 3' - 2" | 2' - 10" |
| 7512 Thermal French & Sash 36x80 Ovolo Raised Panel | Thermal Sash TDL - Twelve Lite - Single Panel | 6' - 8" | 7512 | 3 | 0 | 2 | 6' - 10" | 3' - 4" | 3' - 0" |
| 7512 Thermal French & Sash 36x84 Ovolo Raised Panel | Thermal Sash TDL - Twelve Lite - Single Panel | 7' - 0" | 7512 | 3 | 0 | 2 | 7' - 2" | 3' - 4" | 3' - 0" |
| 7512 Thermal French & Sash 36x96 Ovolo Raised Panel | Thermal Sash TDL - Twelve Lite - Single Panel | 8' - 0" | 7512 | 3 | 0 | 2 | 8' - 2" | 3' - 4" | 3' - 0" |
| 7512 Thermal French & Sash 38x80 Ovolo Raised Panel | Thermal Sash TDL - Twelve Lite - Single Panel | 6' - 8" | 7512 | 3 | 0 | 2 | 6' - 10" | 3' - 6" | 3' - 2" |
| 7512 Thermal French & Sash 38x84 Ovolo Raised Panel | Thermal Sash TDL - Twelve Lite - Single Panel | 7' - 0" | 7512 | 3 | 0 | 2 | 7' - 2" | 3' - 6" | 3' - 2" |
| 7512 Thermal French & Sash 38x96 Ovolo Raised Panel | Thermal Sash TDL - Twelve Lite - Single Panel | 8' - 0" | 7512 | 3 | 0 | 2 | 8' - 2" | 3' - 6" | 3' - 2" |
| 7512 Thermal French & Sash 40x80 Ovolo Raised Panel | Thermal Sash TDL - Twelve Lite - Single Panel | 6' - 8" | 7512 | 3 | 0 | 2 | 6' - 10" | 3' - 8" | 3' - 4" |
| 7512 Thermal French & Sash 40x84 Ovolo Raised Panel | Thermal Sash TDL - Twelve Lite - Single Panel | 7' - 0" | 7512 | 3 | 0 | 2 | 7' - 2" | 3' - 8" | 3' - 4" |
| 7512 Thermal French & Sash 40x96 Ovolo Raised Panel | Thermal Sash TDL - Twelve Lite - Single Panel | 8' - 0" | 7512 | 3 | 0 | 2 | 8' - 2" | 3' - 8" | 3' - 4" |
| 7512 Thermal French & Sash 42x80 Ovolo Raised Panel | Thermal Sash TDL - Twelve Lite - Single Panel | 6' - 8" | 7512 | 3 | 0 | 2 | 6' - 10" | 3' - 10" | 3' - 6" |
| 7512 Thermal French & Sash 42x84 Ovolo Raised Panel | Thermal Sash TDL - Twelve Lite - Single Panel | 7' - 0" | 7512 | 3 | 0 | 2 | 7' - 2" | 3' - 10" | 3' - 6" |
| 7512 Thermal French & Sash 42x96 Ovolo Raised Panel | Thermal Sash TDL - Twelve Lite - Single Panel | 8' - 0" | 7512 | 3 | 0 | 2 | 8' - 2" | 3' - 10" | 3' - 6" |
| 7521 Thermal French & Sash 30x80 Ovolo Raised Panel | Thermal Sash TDL - Single Lite - Two Panel | 6' - 8" | 7521 | 0 | 1 | 0 | 6' - 10" | 2' - 10" | 2' - 6" |
| 7521 Thermal French & Sash 30x84 Ovolo Raised Panel | Thermal Sash TDL - Single Lite - Two Panel | 7' - 0" | 7521 | 0 | 1 | 0 | 7' - 2" | 2' - 10" | 2' - 6" |
| 7521 Thermal French & Sash 30x96 Ovolo Raised Panel | Thermal Sash TDL - Single Lite - Two Panel | 8' - 0" | 7521 | 0 | 1 | 0 | 8' - 2" | 2' - 10" | 2' - 6" |
| 7521 Thermal French & Sash 32x80 Ovolo Raised Panel | Thermal Sash TDL - Single Lite - Two Panel | 6' - 8" | 7521 | 0 | 1 | 0 | 6' - 10" | 3' - 0" | 2' - 8" |
| 7521 Thermal French & Sash 32x84 Ovolo Raised Panel | Thermal Sash TDL - Single Lite - Two Panel | 7' - 0" | 7521 | 0 | 1 | 0 | 7' - 2" | 3' - 0" | 2' - 8" |
| 7521 Thermal French & Sash 32x96 Ovolo Raised Panel | Thermal Sash TDL - Single Lite - Two Panel | 8' - 0" | 7521 | 0 | 1 | 0 | 8' - 2" | 3' - 0" | 2' - 8" |
| 7521 Thermal French & Sash 34x80 Ovolo Raised Panel | Thermal Sash TDL - Single Lite - Two Panel | 6' - 8" | 7521 | 0 | 1 | 0 | 6' - 10" | 3' - 2" | 2' - 10" |
| 7521 Thermal French & Sash 34x84 Ovolo Raised Panel | Thermal Sash TDL - Single Lite - Two Panel | 7' - 0" | 7521 | 0 | 1 | 0 | 7' - 2" | 3' - 2" | 2' - 10" |
| 7521 Thermal French & Sash 34x96 Ovolo Raised Panel | Thermal Sash TDL - Single Lite - Two Panel | 8' - 0" | 7521 | 0 | 1 | 0 | 8' - 2" | 3' - 2" | 2' - 10" |
| 7521 Thermal French & Sash 36x80 Ovolo Raised Panel | Thermal Sash TDL - Single Lite - Two Panel | 6' - 8" | 7521 | 0 | 1 | 0 | 6' - 10" | 3' - 4" | 3' - 0" |
| 7521 Thermal French & Sash 36x84 Ovolo Raised Panel | Thermal Sash TDL - Single Lite - Two Panel | 7' - 0" | 7521 | 0 | 1 | 0 | 7' - 2" | 3' - 4" | 3' - 0" |
| 7521 Thermal French & Sash 36x96 Ovolo Raised Panel | Thermal Sash TDL - Single Lite - Two Panel | 8' - 0" | 7521 | 0 | 1 | 0 | 8' - 2" | 3' - 4" | 3' - 0" |
| 7521 Thermal French & Sash 38x80 Ovolo Raised Panel | Thermal Sash TDL - Single Lite - Two Panel | 6' - 8" | 7521 | 0 | 1 | 0 | 6' - 10" | 3' - 6" | 3' - 2" |
| 7521 Thermal French & Sash 38x84 Ovolo Raised Panel | Thermal Sash TDL - Single Lite - Two Panel | 7' - 0" | 7521 | 0 | 1 | 0 | 7' - 2" | 3' - 6" | 3' - 2" |
| 7521 Thermal French & Sash 38x96 Ovolo Raised Panel | Thermal Sash TDL - Single Lite - Two Panel | 8' - 0" | 7521 | 0 | 1 | 0 | 8' - 2" | 3' - 6" | 3' - 2" |
| 7521 Thermal French & Sash 40x80 Ovolo Raised Panel | Thermal Sash TDL - Single Lite - Two Panel | 6' - 8" | 7521 | 0 | 1 | 0 | 6' - 10" | 3' - 8" | 3' - 4" |
| 7521 Thermal French & Sash 40x84 Ovolo Raised Panel | Thermal Sash TDL - Single Lite - Two Panel | 7' - 0" | 7521 | 0 | 1 | 0 | 7' - 2" | 3' - 8" | 3' - 4" |
| 7521 Thermal French & Sash 40x96 Ovolo Raised Panel | Thermal Sash TDL - Single Lite - Two Panel | 8' - 0" | 7521 | 0 | 1 | 0 | 8' - 2" | 3' - 8" | 3' - 4" |
| 7521 Thermal French & Sash 42x80 Ovolo Raised Panel | Thermal Sash TDL - Single Lite - Two Panel | 6' - 8" | 7521 | 0 | 1 | 0 | 6' - 10" | 3' - 10" | 3' - 6" |
| 7521 Thermal French & Sash 42x84 Ovolo Raised Panel | Thermal Sash TDL - Single Lite - Two Panel | 7' - 0" | 7521 | 0 | 1 | 0 | 7' - 2" | 3' - 10" | 3' - 6" |
| 7521 Thermal French & Sash 42x96 Ovolo Raised Panel | Thermal Sash TDL - Single Lite - Two Panel | 8' - 0" | 7521 | 0 | 1 | 0 | 8' - 2" | 3' - 10" | 3' - 6" |
| 7522 Thermal French & Sash 30x80 Ovolo Raised Panel | Thermal Sash TDL - Twelve Lite - Two Panel | 6' - 8" | 7522 | 3 | 1 | 2 | 6' - 10" | 2' - 10" | 2' - 6" |
| 7522 Thermal French & Sash 30x84 Ovolo Raised Panel | Thermal Sash TDL - Twelve Lite - Two Panel | 7' - 0" | 7522 | 3 | 1 | 2 | 7' - 2" | 2' - 10" | 2' - 6" |
| 7522 Thermal French & Sash 30x96 Ovolo Raised Panel | Thermal Sash TDL - Twelve Lite - Two Panel | 8' - 0" | 7522 | 3 | 1 | 2 | 8' - 2" | 2' - 10" | 2' - 6" |
| 7522 Thermal French & Sash 32x80 Ovolo Raised Panel | Thermal Sash TDL - Twelve Lite - Two Panel | 6' - 8" | 7522 | 3 | 1 | 2 | 6' - 10" | 3' - 0" | 2' - 8" |
| 7522 Thermal French & Sash 32x84 Ovolo Raised Panel | Thermal Sash TDL - Twelve Lite - Two Panel | 7' - 0" | 7522 | 3 | 1 | 2 | 7' - 2" | 3' - 0" | 2' - 8" |
| 7522 Thermal French & Sash 32x96 Ovolo Raised Panel | Thermal Sash TDL - Twelve Lite - Two Panel | 8' - 0" | 7522 | 3 | 1 | 2 | 8' - 2" | 3' - 0" | 2' - 8" |
| 7522 Thermal French & Sash 34x80 Ovolo Raised Panel | Thermal Sash TDL - Twelve Lite - Two Panel | 6' - 8" | 7522 | 3 | 1 | 2 | 6' - 10" | 3' - 2" | 2' - 10" |
| 7522 Thermal French & Sash 34x84 Ovolo Raised Panel | Thermal Sash TDL - Twelve Lite - Two Panel | 7' - 0" | 7522 | 3 | 1 | 2 | 7' - 2" | 3' - 2" | 2' - 10" |
| 7522 Thermal French & Sash 34x96 Ovolo Raised Panel | Thermal Sash TDL - Twelve Lite - Two Panel | 8' - 0" | 7522 | 3 | 1 | 2 | 8' - 2" | 3' - 2" | 2' - 10" |
| 7522 Thermal French & Sash 36x80 Ovolo Raised Panel | Thermal Sash TDL - Twelve Lite - Two Panel | 6' - 8" | 7522 | 3 | 1 | 2 | 6' - 10" | 3' - 4" | 3' - 0" |
| 7522 Thermal French & Sash 36x84 Ovolo Raised Panel | Thermal Sash TDL - Twelve Lite - Two Panel | 7' - 0" | 7522 | 3 | 1 | 2 | 7' - 2" | 3' - 4" | 3' - 0" |
| 7522 Thermal French & Sash 36x96 Ovolo Raised Panel | Thermal Sash TDL - Twelve Lite - Two Panel | 8' - 0" | 7522 | 3 | 1 | 2 | 8' - 2" | 3' - 4" | 3' - 0" |
| 7522 Thermal French & Sash 38x80 Ovolo Raised Panel | Thermal Sash TDL - Twelve Lite - Two Panel | 6' - 8" | 7522 | 3 | 1 | 2 | 6' - 10" | 3' - 6" | 3' - 2" |
| 7522 Thermal French & Sash 38x84 Ovolo Raised Panel | Thermal Sash TDL - Twelve Lite - Two Panel | 7' - 0" | 7522 | 3 | 1 | 2 | 7' - 2" | 3' - 6" | 3' - 2" |
| 7522 Thermal French & Sash 38x96 Ovolo Raised Panel | Thermal Sash TDL - Twelve Lite - Two Panel | 8' - 0" | 7522 | 3 | 1 | 2 | 8' - 2" | 3' - 6" | 3' - 2" |
| 7522 Thermal French & Sash 40x80 Ovolo Raised Panel | Thermal Sash TDL - Twelve Lite - Two Panel | 6' - 8" | 7522 | 3 | 1 | 2 | 6' - 10" | 3' - 8" | 3' - 4" |
| 7522 Thermal French & Sash 40x84 Ovolo Raised Panel | Thermal Sash TDL - Twelve Lite - Two Panel | 7' - 0" | 7522 | 3 | 1 | 2 | 7' - 2" | 3' - 8" | 3' - 4" |
| 7522 Thermal French & Sash 40x96 Ovolo Raised Panel | Thermal Sash TDL - Twelve Lite - Two Panel | 8' - 0" | 7522 | 3 | 1 | 2 | 8' - 2" | 3' - 8" | 3' - 4" |
| 7522 Thermal French & Sash 42x80 Ovolo Raised Panel | Thermal Sash TDL - Twelve Lite - Two Panel | 6' - 8" | 7522 | 3 | 1 | 2 | 6' - 10" | 3' - 10" | 3' - 6" |
| 7522 Thermal French & Sash 42x84 Ovolo Raised Panel | Thermal Sash TDL - Twelve Lite - Two Panel | 7' - 0" | 7522 | 3 | 1 | 2 | 7' - 2" | 3' - 10" | 3' - 6" |
| 7522 Thermal French & Sash 42x96 Ovolo Raised Panel | Thermal Sash TDL - Twelve Lite - Two Panel | 8' - 0" | 7522 | 3 | 1 | 2 | 8' - 2" | 3' - 10" | 3' - 6" |
| 7524 Exterior Sash 30x80 Ovolo Raised Panel | Therma Sash TDL - Four Lite - Two Panel | 6' - 8" | 7524 | 1 | 1 | 1 | 6' - 10" | 2' - 10" | 2' - 6" |
| 7524 Exterior Sash 30x84 Ovolo Raised Panel | Therma Sash TDL - Four Lite - Two Panel | 7' - 0" | 7524 | 1 | 1 | 1 | 7' - 2" | 2' - 10" | 2' - 6" |
| 7524 Exterior Sash 30x96 Ovolo Raised Panel | Therma Sash TDL - Four Lite - Two Panel | 8' - 0" | 7524 | 1 | 1 | 1 | 8' - 2" | 2' - 10" | 2' - 6" |
| 7524 Exterior Sash 32x80 Ovolo Raised Panel | Therma Sash TDL - Four Lite - Two Panel | 6' - 8" | 7524 | 1 | 1 | 1 | 6' - 10" | 3' - 0" | 2' - 8" |
| 7524 Exterior Sash 32x84 Ovolo Raised Panel | Therma Sash TDL - Four Lite - Two Panel | 7' - 0" | 7524 | 1 | 1 | 1 | 7' - 2" | 3' - 0" | 2' - 8" |
| 7524 Exterior Sash 32x96 Ovolo Raised Panel | Therma Sash TDL - Four Lite - Two Panel | 8' - 0" | 7524 | 1 | 1 | 1 | 8' - 2" | 3' - 0" | 2' - 8" |
| 7524 Exterior Sash 34x80 Ovolo Raised Panel | Therma Sash TDL - Four Lite - Two Panel | 6' - 8" | 7524 | 1 | 1 | 1 | 6' - 10" | 3' - 2" | 2' - 10" |
| 7524 Exterior Sash 34x84 Ovolo Raised Panel | Therma Sash TDL - Four Lite - Two Panel | 7' - 0" | 7524 | 1 | 1 | 1 | 7' - 2" | 3' - 2" | 2' - 10" |
| 7524 Exterior Sash 34x96 Ovolo Raised Panel | Therma Sash TDL - Four Lite - Two Panel | 8' - 0" | 7524 | 1 | 1 | 1 | 8' - 2" | 3' - 2" | 2' - 10" |
| 7524 Exterior Sash 36x80 Ovolo Raised Panel | Therma Sash TDL - Four Lite - Two Panel | 6' - 8" | 7524 | 1 | 1 | 1 | 6' - 10" | 3' - 4" | 3' - 0" |
| 7524 Exterior Sash 36x84 Ovolo Raised Panel | Therma Sash TDL - Four Lite - Two Panel | 7' - 0" | 7524 | 1 | 1 | 1 | 7' - 2" | 3' - 4" | 3' - 0" |
| 7524 Exterior Sash 36x96 Ovolo Raised Panel | Therma Sash TDL - Four Lite - Two Panel | 8' - 0" | 7524 | 1 | 1 | 1 | 8' - 2" | 3' - 4" | 3' - 0" |
| 7524 Exterior Sash 38x80 Ovolo Raised Panel | Therma Sash TDL - Four Lite - Two Panel | 6' - 8" | 7524 | 1 | 1 | 1 | 6' - 10" | 3' - 6" | 3' - 2" |
| 7524 Exterior Sash 38x84 Ovolo Raised Panel | Therma Sash TDL - Four Lite - Two Panel | 7' - 0" | 7524 | 1 | 1 | 1 | 7' - 2" | 3' - 6" | 3' - 2" |
| 7524 Exterior Sash 38x96 Ovolo Raised Panel | Therma Sash TDL - Four Lite - Two Panel | 8' - 0" | 7524 | 1 | 1 | 1 | 8' - 2" | 3' - 6" | 3' - 2" |
| 7524 Exterior Sash 40x80 Ovolo Raised Panel | Therma Sash TDL - Four Lite - Two Panel | 6' - 8" | 7524 | 1 | 1 | 1 | 6' - 10" | 3' - 8" | 3' - 4" |
| 7524 Exterior Sash 40x84 Ovolo Raised Panel | Therma Sash TDL - Four Lite - Two Panel | 7' - 0" | 7524 | 1 | 1 | 1 | 7' - 2" | 3' - 8" | 3' - 4" |
| 7524 Exterior Sash 40x96 Ovolo Raised Panel | Therma Sash TDL - Four Lite - Two Panel | 8' - 0" | 7524 | 1 | 1 | 1 | 8' - 2" | 3' - 8" | 3' - 4" |
| 7524 Exterior Sash 42x80 Ovolo Raised Panel | Therma Sash TDL - Four Lite - Two Panel | 6' - 8" | 7524 | 1 | 1 | 1 | 6' - 10" | 3' - 10" | 3' - 6" |
| 7524 Exterior Sash 42x84 Ovolo Raised Panel | Therma Sash TDL - Four Lite - Two Panel | 7' - 0" | 7524 | 1 | 1 | 1 | 7' - 2" | 3' - 10" | 3' - 6" |
| 7524 Exterior Sash 42x96 Ovolo Raised Panel | Therma Sash TDL - Four Lite - Two Panel | 8' - 0" | 7524 | 1 | 1 | 1 | 8' - 2" | 3' - 10" | 3' - 6" |
| 7526 Thermal French & Sash 30x80 Ovolo Raised Panel | Thermal Sash TDL - Six Lite - Single Panel | 6' - 8" | 7526 | 2 | 1 | 1 | 6' - 10" | 2' - 10" | 2' - 6" |
| 7526 Thermal French & Sash 30x84 Ovolo Raised Panel | Thermal Sash TDL - Six Lite - Single Panel | 7' - 0" | 7526 | 2 | 1 | 1 | 7' - 2" | 2' - 10" | 2' - 6" |
| 7526 Thermal French & Sash 30x96 Ovolo Raised Panel | Thermal Sash TDL - Six Lite - Single Panel | 8' - 0" | 7526 | 2 | 1 | 1 | 8' - 2" | 2' - 10" | 2' - 6" |
| 7526 Thermal French & Sash 32x80 Ovolo Raised Panel | Thermal Sash TDL - Six Lite - Single Panel | 6' - 8" | 7526 | 2 | 1 | 1 | 6' - 10" | 3' - 0" | 2' - 8" |
| 7526 Thermal French & Sash 32x84 Ovolo Raised Panel | Thermal Sash TDL - Six Lite - Single Panel | 7' - 0" | 7526 | 2 | 1 | 1 | 7' - 2" | 3' - 0" | 2' - 8" |
| 7526 Thermal French & Sash 32x96 Ovolo Raised Panel | Thermal Sash TDL - Six Lite - Single Panel | 8' - 0" | 7526 | 2 | 1 | 1 | 8' - 2" | 3' - 0" | 2' - 8" |
| 7526 Thermal French & Sash 34x80 Ovolo Raised Panel | Thermal Sash TDL - Six Lite - Single Panel | 6' - 8" | 7526 | 2 | 1 | 1 | 6' - 10" | 3' - 2" | 2' - 10" |
| 7526 Thermal French & Sash 34x84 Ovolo Raised Panel | Thermal Sash TDL - Six Lite - Single Panel | 7' - 0" | 7526 | 2 | 1 | 1 | 7' - 2" | 3' - 2" | 2' - 10" |
| 7526 Thermal French & Sash 34x96 Ovolo Raised Panel | Thermal Sash TDL - Six Lite - Single Panel | 8' - 0" | 7526 | 2 | 1 | 1 | 8' - 2" | 3' - 2" | 2' - 10" |
| 7526 Thermal French & Sash 36x80 Ovolo Raised Panel | Thermal Sash TDL - Six Lite - Single Panel | 6' - 8" | 7526 | 2 | 1 | 1 | 6' - 10" | 3' - 4" | 3' - 0" |
| 7526 Thermal French & Sash 36x84 Ovolo Raised Panel | Thermal Sash TDL - Six Lite - Single Panel | 7' - 0" | 7526 | 2 | 1 | 1 | 7' - 2" | 3' - 4" | 3' - 0" |
| 7526 Thermal French & Sash 36x96 Ovolo Raised Panel | Thermal Sash TDL - Six Lite - Single Panel | 8' - 0" | 7526 | 2 | 1 | 1 | 8' - 2" | 3' - 4" | 3' - 0" |
| 7526 Thermal French & Sash 38x80 Ovolo Raised Panel | Thermal Sash TDL - Six Lite - Single Panel | 6' - 8" | 7526 | 2 | 1 | 1 | 6' - 10" | 3' - 6" | 3' - 2" |
| 7526 Thermal French & Sash 38x84 Ovolo Raised Panel | Thermal Sash TDL - Six Lite - Single Panel | 7' - 0" | 7526 | 2 | 1 | 1 | 7' - 2" | 3' - 6" | 3' - 2" |
| 7526 Thermal French & Sash 38x96 Ovolo Raised Panel | Thermal Sash TDL - Six Lite - Single Panel | 8' - 0" | 7526 | 2 | 1 | 1 | 8' - 2" | 3' - 6" | 3' - 2" |
| 7526 Thermal French & Sash 40x80 Ovolo Raised Panel | Thermal Sash TDL - Six Lite - Single Panel | 6' - 8" | 7526 | 2 | 1 | 1 | 6' - 10" | 3' - 8" | 3' - 4" |
| 7526 Thermal French & Sash 40x84 Ovolo Raised Panel | Thermal Sash TDL - Six Lite - Single Panel | 7' - 0" | 7526 | 2 | 1 | 1 | 7' - 2" | 3' - 8" | 3' - 4" |
| 7526 Thermal French & Sash 40x96 Ovolo Raised Panel | Thermal Sash TDL - Six Lite - Single Panel | 8' - 0" | 7526 | 2 | 1 | 1 | 8' - 2" | 3' - 8" | 3' - 4" |
| 7526 Thermal French & Sash 42x80 Ovolo Raised Panel | Thermal Sash TDL - Six Lite - Single Panel | 6' - 8" | 7526 | 2 | 1 | 1 | 6' - 10" | 3' - 10" | 3' - 6" |
| 7526 Thermal French & Sash 42x84 Ovolo Raised Panel | Thermal Sash TDL - Six Lite - Single Panel | 7' - 0" | 7526 | 2 | 1 | 1 | 7' - 2" | 3' - 10" | 3' - 6" |
| 7526 Thermal French & Sash 42x96 Ovolo Raised Panel | Thermal Sash TDL - Six Lite - Single Panel | 8' - 0" | 7526 | 2 | 1 | 1 | 8' - 2" | 3' - 10" | 3' - 6" |
| 7528 Thermal French & Sash 30x80 Ovolo Raised Panel | Thermal Sash TDL - Eight Lite - Single Panel | 6' - 8" | 7528 | 3 | 1 | 1 | 6' - 10" | 2' - 10" | 2' - 6" |
| 7528 Thermal French & Sash 30x84 Ovolo Raised Panel | Thermal Sash TDL - Eight Lite - Single Panel | 7' - 0" | 7528 | 3 | 1 | 1 | 7' - 2" | 2' - 10" | 2' - 6" |
| 7528 Thermal French & Sash 30x96 Ovolo Raised Panel | Thermal Sash TDL - Eight Lite - Single Panel | 8' - 0" | 7528 | 3 | 1 | 1 | 8' - 2" | 2' - 10" | 2' - 6" |
| 7528 Thermal French & Sash 32x80 Ovolo Raised Panel | Thermal Sash TDL - Eight Lite - Single Panel | 6' - 8" | 7528 | 3 | 1 | 1 | 6' - 10" | 3' - 0" | 2' - 8" |
| 7528 Thermal French & Sash 32x84 Ovolo Raised Panel | Thermal Sash TDL - Eight Lite - Single Panel | 7' - 0" | 7528 | 3 | 1 | 1 | 7' - 2" | 3' - 0" | 2' - 8" |
| 7528 Thermal French & Sash 32x96 Ovolo Raised Panel | Thermal Sash TDL - Eight Lite - Single Panel | 8' - 0" | 7528 | 3 | 1 | 1 | 8' - 2" | 3' - 0" | 2' - 8" |
| 7528 Thermal French & Sash 34x80 Ovolo Raised Panel | Thermal Sash TDL - Eight Lite - Single Panel | 6' - 8" | 7528 | 3 | 1 | 1 | 6' - 10" | 3' - 2" | 2' - 10" |
| 7528 Thermal French & Sash 34x84 Ovolo Raised Panel | Thermal Sash TDL - Eight Lite - Single Panel | 7' - 0" | 7528 | 3 | 1 | 1 | 7' - 2" | 3' - 2" | 2' - 10" |
| 7528 Thermal French & Sash 34x96 Ovolo Raised Panel | Thermal Sash TDL - Eight Lite - Single Panel | 8' - 0" | 7528 | 3 | 1 | 1 | 8' - 2" | 3' - 2" | 2' - 10" |
| 7528 Thermal French & Sash 36x80 Ovolo Raised Panel | Thermal Sash TDL - Eight Lite - Single Panel | 6' - 8" | 7528 | 3 | 1 | 1 | 6' - 10" | 3' - 4" | 3' - 0" |
| 7528 Thermal French & Sash 36x84 Ovolo Raised Panel | Thermal Sash TDL - Eight Lite - Single Panel | 7' - 0" | 7528 | 3 | 1 | 1 | 7' - 2" | 3' - 4" | 3' - 0" |
| 7528 Thermal French & Sash 36x96 Ovolo Raised Panel | Thermal Sash TDL - Eight Lite - Single Panel | 8' - 0" | 7528 | 3 | 1 | 1 | 8' - 2" | 3' - 4" | 3' - 0" |
| 7528 Thermal French & Sash 38x80 Ovolo Raised Panel | Thermal Sash TDL - Eight Lite - Single Panel | 6' - 8" | 7528 | 3 | 1 | 1 | 6' - 10" | 3' - 6" | 3' - 2" |
| 7528 Thermal French & Sash 38x84 Ovolo Raised Panel | Thermal Sash TDL - Eight Lite - Single Panel | 7' - 0" | 7528 | 3 | 1 | 1 | 7' - 2" | 3' - 6" | 3' - 2" |
| 7528 Thermal French & Sash 38x96 Ovolo Raised Panel | Thermal Sash TDL - Eight Lite - Single Panel | 8' - 0" | 7528 | 3 | 1 | 1 | 8' - 2" | 3' - 6" | 3' - 2" |
| 7528 Thermal French & Sash 40x80 Ovolo Raised Panel | Thermal Sash TDL - Eight Lite - Single Panel | 6' - 8" | 7528 | 3 | 1 | 1 | 6' - 10" | 3' - 8" | 3' - 4" |
| 7528 Thermal French & Sash 40x84 Ovolo Raised Panel | Thermal Sash TDL - Eight Lite - Single Panel | 7' - 0" | 7528 | 3 | 1 | 1 | 7' - 2" | 3' - 8" | 3' - 4" |
| 7528 Thermal French & Sash 40x96 Ovolo Raised Panel | Thermal Sash TDL - Eight Lite - Single Panel | 8' - 0" | 7528 | 3 | 1 | 1 | 8' - 2" | 3' - 8" | 3' - 4" |
| 7528 Thermal French & Sash 42x80 Ovolo Raised Panel | Thermal Sash TDL - Eight Lite - Single Panel | 6' - 8" | 7528 | 3 | 1 | 1 | 6' - 10" | 3' - 10" | 3' - 6" |
| 7528 Thermal French & Sash 42x84 Ovolo Raised Panel | Thermal Sash TDL - Eight Lite - Single Panel | 7' - 0" | 7528 | 3 | 1 | 1 | 7' - 2" | 3' - 10" | 3' - 6" |
| 7528 Thermal French & Sash 42x96 Ovolo Raised Panel | Thermal Sash TDL - Eight Lite - Single Panel | 8' - 0" | 7528 | 3 | 1 | 1 | 8' - 2" | 3' - 10" | 3' - 6" |
| 37504 Thermal French & Sash 30x80 Ovolo Raised Panel | Thermal Sash SDL - Four Lite - Single Panel | 6' - 8" | 37504 | 1 | 0 | 1 | 6' - 10" | 2' - 10" | 2' - 6" |
| 37504 Thermal French & Sash 30x84 Ovolo Raised Panel | Thermal Sash SDL - Four Lite - Single Panel | 7' - 0" | 37504 | 1 | 0 | 1 | 7' - 2" | 2' - 10" | 2' - 6" |
| 37504 Thermal French & Sash 30x96 Ovolo Raised Panel | Thermal Sash SDL - Four Lite - Single Panel | 8' - 0" | 37504 | 1 | 0 | 1 | 8' - 2" | 2' - 10" | 2' - 6" |
| 37504 Thermal French & Sash 32x80 Ovolo Raised Panel | Thermal Sash SDL - Four Lite - Single Panel | 6' - 8" | 37504 | 1 | 0 | 1 | 6' - 10" | 3' - 0" | 2' - 8" |
| 37504 Thermal French & Sash 32x84 Ovolo Raised Panel | Thermal Sash SDL - Four Lite - Single Panel | 7' - 0" | 37504 | 1 | 0 | 1 | 7' - 2" | 3' - 0" | 2' - 8" |
| 37504 Thermal French & Sash 32x96 Ovolo Raised Panel | Thermal Sash SDL - Four Lite - Single Panel | 8' - 0" | 37504 | 1 | 0 | 1 | 8' - 2" | 3' - 0" | 2' - 8" |
| 37504 Thermal French & Sash 34x80 Ovolo Raised Panel | Thermal Sash SDL - Four Lite - Single Panel | 6' - 8" | 37504 | 1 | 0 | 1 | 6' - 10" | 3' - 2" | 2' - 10" |
| 37504 Thermal French & Sash 34x84 Ovolo Raised Panel | Thermal Sash SDL - Four Lite - Single Panel | 7' - 0" | 37504 | 1 | 0 | 1 | 7' - 2" | 3' - 2" | 2' - 10" |
| 37504 Thermal French & Sash 34x96 Ovolo Raised Panel | Thermal Sash SDL - Four Lite - Single Panel | 8' - 0" | 37504 | 1 | 0 | 1 | 8' - 2" | 3' - 2" | 2' - 10" |
| 37504 Thermal French & Sash 36x80 Ovolo Raised Panel | Thermal Sash SDL - Four Lite - Single Panel | 6' - 8" | 37504 | 1 | 0 | 1 | 6' - 10" | 3' - 4" | 3' - 0" |
| 37504 Thermal French & Sash 36x84 Ovolo Raised Panel | Thermal Sash SDL - Four Lite - Single Panel | 7' - 0" | 37504 | 1 | 0 | 1 | 7' - 2" | 3' - 4" | 3' - 0" |
| 37504 Thermal French & Sash 36x96 Ovolo Raised Panel | Thermal Sash SDL - Four Lite - Single Panel | 8' - 0" | 37504 | 1 | 0 | 1 | 8' - 2" | 3' - 4" | 3' - 0" |
| 37504 Thermal French & Sash 38x80 Ovolo Raised Panel | Thermal Sash SDL - Four Lite - Single Panel | 6' - 8" | 37504 | 1 | 0 | 1 | 6' - 10" | 3' - 6" | 3' - 2" |
| 37504 Thermal French & Sash 38x84 Ovolo Raised Panel | Thermal Sash SDL - Four Lite - Single Panel | 7' - 0" | 37504 | 1 | 0 | 1 | 7' - 2" | 3' - 6" | 3' - 2" |
| 37504 Thermal French & Sash 38x96 Ovolo Raised Panel | Thermal Sash SDL - Four Lite - Single Panel | 8' - 0" | 37504 | 1 | 0 | 1 | 8' - 2" | 3' - 6" | 3' - 2" |
| 37504 Thermal French & Sash 40x80 Ovolo Raised Panel | Thermal Sash SDL - Four Lite - Single Panel | 6' - 8" | 37504 | 1 | 0 | 1 | 6' - 10" | 3' - 8" | 3' - 4" |
| 37504 Thermal French & Sash 40x84 Ovolo Raised Panel | Thermal Sash SDL - Four Lite - Single Panel | 7' - 0" | 37504 | 1 | 0 | 1 | 7' - 2" | 3' - 8" | 3' - 4" |
| 37504 Thermal French & Sash 40x96 Ovolo Raised Panel | Thermal Sash SDL - Four Lite - Single Panel | 8' - 0" | 37504 | 1 | 0 | 1 | 8' - 2" | 3' - 8" | 3' - 4" |
| 37504 Thermal French & Sash 42x80 Ovolo Raised Panel | Thermal Sash SDL - Four Lite - Single Panel | 6' - 8" | 37504 | 1 | 0 | 1 | 6' - 10" | 3' - 10" | 3' - 6" |
| 37504 Thermal French & Sash 42x84 Ovolo Raised Panel | Thermal Sash SDL - Four Lite - Single Panel | 7' - 0" | 37504 | 1 | 0 | 1 | 7' - 2" | 3' - 10" | 3' - 6" |
| 37504 Thermal French & Sash 42x96 Ovolo Raised Panel | Thermal Sash SDL - Four Lite - Single Panel | 8' - 0" | 37504 | 1 | 0 | 1 | 8' - 2" | 3' - 10" | 3' - 6" |
| 37506 Thermal French & Sash 30x80 Ovolo Raised Panel | Thermal Sash SDL - Six Lite - Single Panel | 6' - 8" | 37506 | 2 | 0 | 1 | 6' - 10" | 2' - 10" | 2' - 6" |
| 37506 Thermal French & Sash 30x84 Ovolo Raised Panel | Thermal Sash SDL - Six Lite - Single Panel | 7' - 0" | 37506 | 2 | 0 | 1 | 7' - 2" | 2' - 10" | 2' - 6" |
| 37506 Thermal French & Sash 30x96 Ovolo Raised Panel | Thermal Sash SDL - Six Lite - Single Panel | 8' - 0" | 37506 | 2 | 0 | 1 | 8' - 2" | 2' - 10" | 2' - 6" |
| 37506 Thermal French & Sash 32x80 Ovolo Raised Panel | Thermal Sash SDL - Six Lite - Single Panel | 6' - 8" | 37506 | 2 | 0 | 1 | 6' - 10" | 3' - 0" | 2' - 8" |
| 37506 Thermal French & Sash 32x84 Ovolo Raised Panel | Thermal Sash SDL - Six Lite - Single Panel | 7' - 0" | 37506 | 2 | 0 | 1 | 7' - 2" | 3' - 0" | 2' - 8" |
| 37506 Thermal French & Sash 32x96 Ovolo Raised Panel | Thermal Sash SDL - Six Lite - Single Panel | 8' - 0" | 37506 | 2 | 0 | 1 | 8' - 2" | 3' - 0" | 2' - 8" |
| 37506 Thermal French & Sash 34x80 Ovolo Raised Panel | Thermal Sash SDL - Six Lite - Single Panel | 6' - 8" | 37506 | 2 | 0 | 1 | 6' - 10" | 3' - 2" | 2' - 10" |
| 37506 Thermal French & Sash 34x84 Ovolo Raised Panel | Thermal Sash SDL - Six Lite - Single Panel | 7' - 0" | 37506 | 2 | 0 | 1 | 7' - 2" | 3' - 2" | 2' - 10" |
| 37506 Thermal French & Sash 34x96 Ovolo Raised Panel | Thermal Sash SDL - Six Lite - Single Panel | 8' - 0" | 37506 | 2 | 0 | 1 | 8' - 2" | 3' - 2" | 2' - 10" |
| 37506 Thermal French & Sash 36x80 Ovolo Raised Panel | Thermal Sash SDL - Six Lite - Single Panel | 6' - 8" | 37506 | 2 | 0 | 1 | 6' - 10" | 3' - 4" | 3' - 0" |
| 37506 Thermal French & Sash 36x84 Ovolo Raised Panel | Thermal Sash SDL - Six Lite - Single Panel | 7' - 0" | 37506 | 2 | 0 | 1 | 7' - 2" | 3' - 4" | 3' - 0" |
| 37506 Thermal French & Sash 36x96 Ovolo Raised Panel | Thermal Sash SDL - Six Lite - Single Panel | 8' - 0" | 37506 | 2 | 0 | 1 | 8' - 2" | 3' - 4" | 3' - 0" |
| 37506 Thermal French & Sash 38x80 Ovolo Raised Panel | Thermal Sash SDL - Six Lite - Single Panel | 6' - 8" | 37506 | 2 | 0 | 1 | 6' - 10" | 3' - 6" | 3' - 2" |
| 37506 Thermal French & Sash 38x84 Ovolo Raised Panel | Thermal Sash SDL - Six Lite - Single Panel | 7' - 0" | 37506 | 2 | 0 | 1 | 7' - 2" | 3' - 6" | 3' - 2" |
| 37506 Thermal French & Sash 38x96 Ovolo Raised Panel | Thermal Sash SDL - Six Lite - Single Panel | 8' - 0" | 37506 | 2 | 0 | 1 | 8' - 2" | 3' - 6" | 3' - 2" |
| 37506 Thermal French & Sash 40x80 Ovolo Raised Panel | Thermal Sash SDL - Six Lite - Single Panel | 6' - 8" | 37506 | 2 | 0 | 1 | 6' - 10" | 3' - 8" | 3' - 4" |
| 37506 Thermal French & Sash 40x84 Ovolo Raised Panel | Thermal Sash SDL - Six Lite - Single Panel | 7' - 0" | 37506 | 2 | 0 | 1 | 7' - 2" | 3' - 8" | 3' - 4" |
| 37506 Thermal French & Sash 40x96 Ovolo Raised Panel | Thermal Sash SDL - Six Lite - Single Panel | 8' - 0" | 37506 | 2 | 0 | 1 | 8' - 2" | 3' - 8" | 3' - 4" |
| 37506 Thermal French & Sash 42x80 Ovolo Raised Panel | Thermal Sash SDL - Six Lite - Single Panel | 6' - 8" | 37506 | 2 | 0 | 1 | 6' - 10" | 3' - 10" | 3' - 6" |
| 37506 Thermal French & Sash 42x84 Ovolo Raised Panel | Thermal Sash SDL - Six Lite - Single Panel | 7' - 0" | 37506 | 2 | 0 | 1 | 7' - 2" | 3' - 10" | 3' - 6" |
| 37506 Thermal French & Sash 42x96 Ovolo Raised Panel | Thermal Sash SDL - Six Lite - Single Panel | 8' - 0" | 37506 | 2 | 0 | 1 | 8' - 2" | 3' - 10" | 3' - 6" |
| 37508 Thermal French & Sash 30x80 Ovolo Raised Panel | Thermal Sash SDL - Eight Lite - Single Panel | 6' - 8" | 37508 | 3 | 0 | 1 | 6' - 10" | 2' - 10" | 2' - 6" |
| 37508 Thermal French & Sash 30x84 Ovolo Raised Panel | Thermal Sash SDL - Eight Lite - Single Panel | 7' - 0" | 37508 | 3 | 0 | 1 | 7' - 2" | 2' - 10" | 2' - 6" |
| 37508 Thermal French & Sash 30x96 Ovolo Raised Panel | Thermal Sash SDL - Eight Lite - Single Panel | 8' - 0" | 37508 | 3 | 0 | 1 | 8' - 2" | 2' - 10" | 2' - 6" |
| 37508 Thermal French & Sash 32x80 Ovolo Raised Panel | Thermal Sash SDL - Eight Lite - Single Panel | 6' - 8" | 37508 | 3 | 0 | 1 | 6' - 10" | 3' - 0" | 2' - 8" |
| 37508 Thermal French & Sash 32x84 Ovolo Raised Panel | Thermal Sash SDL - Eight Lite - Single Panel | 7' - 0" | 37508 | 3 | 0 | 1 | 7' - 2" | 3' - 0" | 2' - 8" |
| 37508 Thermal French & Sash 32x96 Ovolo Raised Panel | Thermal Sash SDL - Eight Lite - Single Panel | 8' - 0" | 37508 | 3 | 0 | 1 | 8' - 2" | 3' - 0" | 2' - 8" |
| 37508 Thermal French & Sash 34x80 Ovolo Raised Panel | Thermal Sash SDL - Eight Lite - Single Panel | 6' - 8" | 37508 | 3 | 0 | 1 | 6' - 10" | 3' - 2" | 2' - 10" |
| 37508 Thermal French & Sash 34x84 Ovolo Raised Panel | Thermal Sash SDL - Eight Lite - Single Panel | 7' - 0" | 37508 | 3 | 0 | 1 | 7' - 2" | 3' - 2" | 2' - 10" |
| 37508 Thermal French & Sash 34x96 Ovolo Raised Panel | Thermal Sash SDL - Eight Lite - Single Panel | 8' - 0" | 37508 | 3 | 0 | 1 | 8' - 2" | 3' - 2" | 2' - 10" |
| 37508 Thermal French & Sash 36x80 Ovolo Raised Panel | Thermal Sash SDL - Eight Lite - Single Panel | 6' - 8" | 37508 | 3 | 0 | 1 | 6' - 10" | 3' - 4" | 3' - 0" |
| 37508 Thermal French & Sash 36x84 Ovolo Raised Panel | Thermal Sash SDL - Eight Lite - Single Panel | 7' - 0" | 37508 | 3 | 0 | 1 | 7' - 2" | 3' - 4" | 3' - 0" |
| 37508 Thermal French & Sash 36x96 Ovolo Raised Panel | Thermal Sash SDL - Eight Lite - Single Panel | 8' - 0" | 37508 | 3 | 0 | 1 | 8' - 2" | 3' - 4" | 3' - 0" |
| 37508 Thermal French & Sash 38x80 Ovolo Raised Panel | Thermal Sash SDL - Eight Lite - Single Panel | 6' - 8" | 37508 | 3 | 0 | 1 | 6' - 10" | 3' - 6" | 3' - 2" |
| 37508 Thermal French & Sash 38x84 Ovolo Raised Panel | Thermal Sash SDL - Eight Lite - Single Panel | 7' - 0" | 37508 | 3 | 0 | 1 | 7' - 2" | 3' - 6" | 3' - 2" |
| 37508 Thermal French & Sash 38x96 Ovolo Raised Panel | Thermal Sash SDL - Eight Lite - Single Panel | 8' - 0" | 37508 | 3 | 0 | 1 | 8' - 2" | 3' - 6" | 3' - 2" |
| 37508 Thermal French & Sash 40x80 Ovolo Raised Panel | Thermal Sash SDL - Eight Lite - Single Panel | 6' - 8" | 37508 | 3 | 0 | 1 | 6' - 10" | 3' - 8" | 3' - 4" |
| 37508 Thermal French & Sash 40x84 Ovolo Raised Panel | Thermal Sash SDL - Eight Lite - Single Panel | 7' - 0" | 37508 | 3 | 0 | 1 | 7' - 2" | 3' - 8" | 3' - 4" |
| 37508 Thermal French & Sash 40x96 Ovolo Raised Panel | Thermal Sash SDL - Eight Lite - Single Panel | 8' - 0" | 37508 | 3 | 0 | 1 | 8' - 2" | 3' - 8" | 3' - 4" |
| 37508 Thermal French & Sash 42x80 Ovolo Raised Panel | Thermal Sash SDL - Eight Lite - Single Panel | 6' - 8" | 37508 | 3 | 0 | 1 | 6' - 10" | 3' - 10" | 3' - 6" |
| 37508 Thermal French & Sash 42x84 Ovolo Raised Panel | Thermal Sash SDL - Eight Lite - Single Panel | 7' - 0" | 37508 | 3 | 0 | 1 | 7' - 2" | 3' - 10" | 3' - 6" |
| 37508 Thermal French & Sash 42x96 Ovolo Raised Panel | Thermal Sash SDL - Eight Lite - Single Panel | 8' - 0" | 37508 | 3 | 0 | 1 | 8' - 2" | 3' - 10" | 3' - 6" |
| 37512 Thermal French & Sash 30x80 Ovolo Raised Panel | Thermal Sash SDL - Twelve Lite - Single Panel | 6' - 8" | 37512 | 3 | 0 | 2 | 6' - 10" | 2' - 10" | 2' - 6" |
| 37512 Thermal French & Sash 30x84 Ovolo Raised Panel | Thermal Sash SDL - Twelve Lite - Single Panel | 7' - 0" | 37512 | 3 | 0 | 2 | 7' - 2" | 2' - 10" | 2' - 6" |
| 37512 Thermal French & Sash 30x96 Ovolo Raised Panel | Thermal Sash SDL - Twelve Lite - Single Panel | 8' - 0" | 37512 | 3 | 0 | 2 | 8' - 2" | 2' - 10" | 2' - 6" |
| 37512 Thermal French & Sash 32x80 Ovolo Raised Panel | Thermal Sash SDL - Twelve Lite - Single Panel | 6' - 8" | 37512 | 3 | 0 | 2 | 6' - 10" | 3' - 0" | 2' - 8" |
| 37512 Thermal French & Sash 32x84 Ovolo Raised Panel | Thermal Sash SDL - Twelve Lite - Single Panel | 7' - 0" | 37512 | 3 | 0 | 2 | 7' - 2" | 3' - 0" | 2' - 8" |
| 37512 Thermal French & Sash 32x96 Ovolo Raised Panel | Thermal Sash SDL - Twelve Lite - Single Panel | 8' - 0" | 37512 | 3 | 0 | 2 | 8' - 2" | 3' - 0" | 2' - 8" |
| 37512 Thermal French & Sash 34x80 Ovolo Raised Panel | Thermal Sash SDL - Twelve Lite - Single Panel | 6' - 8" | 37512 | 3 | 0 | 2 | 6' - 10" | 3' - 2" | 2' - 10" |
| 37512 Thermal French & Sash 34x84 Ovolo Raised Panel | Thermal Sash SDL - Twelve Lite - Single Panel | 7' - 0" | 37512 | 3 | 0 | 2 | 7' - 2" | 3' - 2" | 2' - 10" |
| 37512 Thermal French & Sash 34x96 Ovolo Raised Panel | Thermal Sash SDL - Twelve Lite - Single Panel | 8' - 0" | 37512 | 3 | 0 | 2 | 8' - 2" | 3' - 2" | 2' - 10" |
| 37512 Thermal French & Sash 36x80 Ovolo Raised Panel | Thermal Sash SDL - Twelve Lite - Single Panel | 6' - 8" | 37512 | 3 | 0 | 2 | 6' - 10" | 3' - 4" | 3' - 0" |
| 37512 Thermal French & Sash 36x84 Ovolo Raised Panel | Thermal Sash SDL - Twelve Lite - Single Panel | 7' - 0" | 37512 | 3 | 0 | 2 | 7' - 2" | 3' - 4" | 3' - 0" |
| 37512 Thermal French & Sash 36x96 Ovolo Raised Panel | Thermal Sash SDL - Twelve Lite - Single Panel | 8' - 0" | 37512 | 3 | 0 | 2 | 8' - 2" | 3' - 4" | 3' - 0" |
| 37512 Thermal French & Sash 38x80 Ovolo Raised Panel | Thermal Sash SDL - Twelve Lite - Single Panel | 6' - 8" | 37512 | 3 | 0 | 2 | 6' - 10" | 3' - 6" | 3' - 2" |
| 37512 Thermal French & Sash 38x84 Ovolo Raised Panel | Thermal Sash SDL - Twelve Lite - Single Panel | 7' - 0" | 37512 | 3 | 0 | 2 | 7' - 2" | 3' - 6" | 3' - 2" |
| 37512 Thermal French & Sash 38x96 Ovolo Raised Panel | Thermal Sash SDL - Twelve Lite - Single Panel | 8' - 0" | 37512 | 3 | 0 | 2 | 8' - 2" | 3' - 6" | 3' - 2" |
| 37512 Thermal French & Sash 40x80 Ovolo Raised Panel | Thermal Sash SDL - Twelve Lite - Single Panel | 6' - 8" | 37512 | 3 | 0 | 2 | 6' - 10" | 3' - 8" | 3' - 4" |
| 37512 Thermal French & Sash 40x84 Ovolo Raised Panel | Thermal Sash SDL - Twelve Lite - Single Panel | 7' - 0" | 37512 | 3 | 0 | 2 | 7' - 2" | 3' - 8" | 3' - 4" |
| 37512 Thermal French & Sash 40x96 Ovolo Raised Panel | Thermal Sash SDL - Twelve Lite - Single Panel | 8' - 0" | 37512 | 3 | 0 | 2 | 8' - 2" | 3' - 8" | 3' - 4" |
| 37512 Thermal French & Sash 42x80 Ovolo Raised Panel | Thermal Sash SDL - Twelve Lite - Single Panel | 6' - 8" | 37512 | 3 | 0 | 2 | 6' - 10" | 3' - 10" | 3' - 6" |
| 37512 Thermal French & Sash 42x84 Ovolo Raised Panel | Thermal Sash SDL - Twelve Lite - Single Panel | 7' - 0" | 37512 | 3 | 0 | 2 | 7' - 2" | 3' - 10" | 3' - 6" |
| 37512 Thermal French & Sash 42x96 Ovolo Raised Panel | Thermal Sash SDL - Twelve Lite - Single Panel | 8' - 0" | 37512 | 3 | 0 | 2 | 8' - 2" | 3' - 10" | 3' - 6" |
| 37522 Thermal French & Sash 30x80 Ovolo Raised Panel | Thermal Sash TDL - Twelve Lite - Two Panel | 6' - 8" | 37522 | 3 | 1 | 2 | 6' - 10" | 2' - 10" | 2' - 6" |
| 37522 Thermal French & Sash 30x84 Ovolo Raised Panel | Thermal Sash TDL - Twelve Lite - Two Panel | 7' - 0" | 37522 | 3 | 1 | 2 | 7' - 2" | 2' - 10" | 2' - 6" |
| 37522 Thermal French & Sash 30x96 Ovolo Raised Panel | Thermal Sash TDL - Twelve Lite - Two Panel | 8' - 0" | 37522 | 3 | 1 | 2 | 8' - 2" | 2' - 10" | 2' - 6" |
| 37522 Thermal French & Sash 32x80 Ovolo Raised Panel | Thermal Sash TDL - Twelve Lite - Two Panel | 6' - 8" | 37522 | 3 | 1 | 2 | 6' - 10" | 3' - 0" | 2' - 8" |
| 37522 Thermal French & Sash 32x84 Ovolo Raised Panel | Thermal Sash TDL - Twelve Lite - Two Panel | 7' - 0" | 37522 | 3 | 1 | 2 | 7' - 2" | 3' - 0" | 2' - 8" |
| 37522 Thermal French & Sash 32x96 Ovolo Raised Panel | Thermal Sash TDL - Twelve Lite - Two Panel | 8' - 0" | 37522 | 3 | 1 | 2 | 8' - 2" | 3' - 0" | 2' - 8" |
| 37522 Thermal French & Sash 34x80 Ovolo Raised Panel | Thermal Sash TDL - Twelve Lite - Two Panel | 6' - 8" | 37522 | 3 | 1 | 2 | 6' - 10" | 3' - 2" | 2' - 10" |
| 37522 Thermal French & Sash 34x84 Ovolo Raised Panel | Thermal Sash TDL - Twelve Lite - Two Panel | 7' - 0" | 37522 | 3 | 1 | 2 | 7' - 2" | 3' - 2" | 2' - 10" |
| 37522 Thermal French & Sash 34x96 Ovolo Raised Panel | Thermal Sash TDL - Twelve Lite - Two Panel | 8' - 0" | 37522 | 3 | 1 | 2 | 8' - 2" | 3' - 2" | 2' - 10" |
| 37522 Thermal French & Sash 36x80 Ovolo Raised Panel | Thermal Sash TDL - Twelve Lite - Two Panel | 6' - 8" | 37522 | 3 | 1 | 2 | 6' - 10" | 3' - 4" | 3' - 0" |
| 37522 Thermal French & Sash 36x84 Ovolo Raised Panel | Thermal Sash TDL - Twelve Lite - Two Panel | 7' - 0" | 37522 | 3 | 1 | 2 | 7' - 2" | 3' - 4" | 3' - 0" |
| 37522 Thermal French & Sash 36x96 Ovolo Raised Panel | Thermal Sash TDL - Twelve Lite - Two Panel | 8' - 0" | 37522 | 3 | 1 | 2 | 8' - 2" | 3' - 4" | 3' - 0" |
| 37522 Thermal French & Sash 38x80 Ovolo Raised Panel | Thermal Sash TDL - Twelve Lite - Two Panel | 6' - 8" | 37522 | 3 | 1 | 2 | 6' - 10" | 3' - 6" | 3' - 2" |
| 37522 Thermal French & Sash 38x84 Ovolo Raised Panel | Thermal Sash TDL - Twelve Lite - Two Panel | 7' - 0" | 37522 | 3 | 1 | 2 | 7' - 2" | 3' - 6" | 3' - 2" |
| 37522 Thermal French & Sash 38x96 Ovolo Raised Panel | Thermal Sash TDL - Twelve Lite - Two Panel | 8' - 0" | 37522 | 3 | 1 | 2 | 8' - 2" | 3' - 6" | 3' - 2" |
| 37522 Thermal French & Sash 40x80 Ovolo Raised Panel | Thermal Sash TDL - Twelve Lite - Two Panel | 6' - 8" | 37522 | 3 | 1 | 2 | 6' - 10" | 3' - 8" | 3' - 4" |
| 37522 Thermal French & Sash 40x84 Ovolo Raised Panel | Thermal Sash TDL - Twelve Lite - Two Panel | 7' - 0" | 37522 | 3 | 1 | 2 | 7' - 2" | 3' - 8" | 3' - 4" |
| 37522 Thermal French & Sash 40x96 Ovolo Raised Panel | Thermal Sash TDL - Twelve Lite - Two Panel | 8' - 0" | 37522 | 3 | 1 | 2 | 8' - 2" | 3' - 8" | 3' - 4" |
| 37522 Thermal French & Sash 42x80 Ovolo Raised Panel | Thermal Sash TDL - Twelve Lite - Two Panel | 6' - 8" | 37522 | 3 | 1 | 2 | 6' - 10" | 3' - 10" | 3' - 6" |
| 37522 Thermal French & Sash 42x84 Ovolo Raised Panel | Thermal Sash TDL - Twelve Lite - Two Panel | 7' - 0" | 37522 | 3 | 1 | 2 | 7' - 2" | 3' - 10" | 3' - 6" |
| 37522 Thermal French & Sash 42x96 Ovolo Raised Panel | Thermal Sash TDL - Twelve Lite - Two Panel | 8' - 0" | 37522 | 3 | 1 | 2 | 8' - 2" | 3' - 10" | 3' - 6" |
| 37524 Exterior Sash 30x80 Ovolo Raised Panel | Therma Sash SDL - Four Lite - Two Panel | 6' - 8" | 37524 | 1 | 1 | 1 | 6' - 10" | 2' - 10" | 2' - 6" |
| 37524 Exterior Sash 30x84 Ovolo Raised Panel | Therma Sash SDL - Four Lite - Two Panel | 7' - 0" | 37524 | 1 | 1 | 1 | 7' - 2" | 2' - 10" | 2' - 6" |
| 37524 Exterior Sash 30x96 Ovolo Raised Panel | Therma Sash SDL - Four Lite - Two Panel | 8' - 0" | 37524 | 1 | 1 | 1 | 8' - 2" | 2' - 10" | 2' - 6" |
| 37524 Exterior Sash 32x80 Ovolo Raised Panel | Therma Sash SDL - Four Lite - Two Panel | 6' - 8" | 37524 | 1 | 1 | 1 | 6' - 10" | 3' - 0" | 2' - 8" |
| 37524 Exterior Sash 32x84 Ovolo Raised Panel | Therma Sash SDL - Four Lite - Two Panel | 7' - 0" | 37524 | 1 | 1 | 1 | 7' - 2" | 3' - 0" | 2' - 8" |
| 37524 Exterior Sash 32x96 Ovolo Raised Panel | Therma Sash SDL - Four Lite - Two Panel | 8' - 0" | 37524 | 1 | 1 | 1 | 8' - 2" | 3' - 0" | 2' - 8" |
| 37524 Exterior Sash 34x80 Ovolo Raised Panel | Therma Sash SDL - Four Lite - Two Panel | 6' - 8" | 37524 | 1 | 1 | 1 | 6' - 10" | 3' - 2" | 2' - 10" |
| 37524 Exterior Sash 34x84 Ovolo Raised Panel | Therma Sash SDL - Four Lite - Two Panel | 7' - 0" | 37524 | 1 | 1 | 1 | 7' - 2" | 3' - 2" | 2' - 10" |
| 37524 Exterior Sash 34x96 Ovolo Raised Panel | Therma Sash SDL - Four Lite - Two Panel | 8' - 0" | 37524 | 1 | 1 | 1 | 8' - 2" | 3' - 2" | 2' - 10" |
| 37524 Exterior Sash 36x80 Ovolo Raised Panel | Therma Sash SDL - Four Lite - Two Panel | 6' - 8" | 37524 | 1 | 1 | 1 | 6' - 10" | 3' - 4" | 3' - 0" |
| 37524 Exterior Sash 36x84 Ovolo Raised Panel | Therma Sash SDL - Four Lite - Two Panel | 7' - 0" | 37524 | 1 | 1 | 1 | 7' - 2" | 3' - 4" | 3' - 0" |
| 37524 Exterior Sash 36x96 Ovolo Raised Panel | Therma Sash SDL - Four Lite - Two Panel | 8' - 0" | 37524 | 1 | 1 | 1 | 8' - 2" | 3' - 4" | 3' - 0" |
| 37524 Exterior Sash 38x80 Ovolo Raised Panel | Therma Sash SDL - Four Lite - Two Panel | 6' - 8" | 37524 | 1 | 1 | 1 | 6' - 10" | 3' - 6" | 3' - 2" |
| 37524 Exterior Sash 38x84 Ovolo Raised Panel | Therma Sash SDL - Four Lite - Two Panel | 7' - 0" | 37524 | 1 | 1 | 1 | 7' - 2" | 3' - 6" | 3' - 2" |
| 37524 Exterior Sash 38x96 Ovolo Raised Panel | Therma Sash SDL - Four Lite - Two Panel | 8' - 0" | 37524 | 1 | 1 | 1 | 8' - 2" | 3' - 6" | 3' - 2" |
| 37524 Exterior Sash 40x80 Ovolo Raised Panel | Therma Sash SDL - Four Lite - Two Panel | 6' - 8" | 37524 | 1 | 1 | 1 | 6' - 10" | 3' - 8" | 3' - 4" |
| 37524 Exterior Sash 40x84 Ovolo Raised Panel | Therma Sash SDL - Four Lite - Two Panel | 7' - 0" | 37524 | 1 | 1 | 1 | 7' - 2" | 3' - 8" | 3' - 4" |
| 37524 Exterior Sash 40x96 Ovolo Raised Panel | Therma Sash SDL - Four Lite - Two Panel | 8' - 0" | 37524 | 1 | 1 | 1 | 8' - 2" | 3' - 8" | 3' - 4" |
| 37524 Exterior Sash 42x80 Ovolo Raised Panel | Therma Sash SDL - Four Lite - Two Panel | 6' - 8" | 37524 | 1 | 1 | 1 | 6' - 10" | 3' - 10" | 3' - 6" |
| 37524 Exterior Sash 42x84 Ovolo Raised Panel | Therma Sash SDL - Four Lite - Two Panel | 7' - 0" | 37524 | 1 | 1 | 1 | 7' - 2" | 3' - 10" | 3' - 6" |
| 37524 Exterior Sash 42x96 Ovolo Raised Panel | Therma Sash SDL - Four Lite - Two Panel | 8' - 0" | 37524 | 1 | 1 | 1 | 8' - 2" | 3' - 10" | 3' - 6" |
| 37526 Thermal French & Sash 30x80 Ovolo Raised Panel | Thermal Sash SDL - Six Lite - Single Panel | 6' - 8" | 37526 | 2 | 1 | 1 | 6' - 10" | 2' - 10" | 2' - 6" |
| 37526 Thermal French & Sash 30x84 Ovolo Raised Panel | Thermal Sash SDL - Six Lite - Single Panel | 7' - 0" | 37526 | 2 | 1 | 1 | 7' - 2" | 2' - 10" | 2' - 6" |
| 37526 Thermal French & Sash 30x96 Ovolo Raised Panel | Thermal Sash SDL - Six Lite - Single Panel | 8' - 0" | 37526 | 2 | 1 | 1 | 8' - 2" | 2' - 10" | 2' - 6" |
| 37526 Thermal French & Sash 32x80 Ovolo Raised Panel | Thermal Sash SDL - Six Lite - Single Panel | 6' - 8" | 37526 | 2 | 1 | 1 | 6' - 10" | 3' - 0" | 2' - 8" |
| 37526 Thermal French & Sash 32x84 Ovolo Raised Panel | Thermal Sash SDL - Six Lite - Single Panel | 7' - 0" | 37526 | 2 | 1 | 1 | 7' - 2" | 3' - 0" | 2' - 8" |
| 37526 Thermal French & Sash 32x96 Ovolo Raised Panel | Thermal Sash SDL - Six Lite - Single Panel | 8' - 0" | 37526 | 2 | 1 | 1 | 8' - 2" | 3' - 0" | 2' - 8" |
| 37526 Thermal French & Sash 34x80 Ovolo Raised Panel | Thermal Sash SDL - Six Lite - Single Panel | 6' - 8" | 37526 | 2 | 1 | 1 | 6' - 10" | 3' - 2" | 2' - 10" |
| 37526 Thermal French & Sash 34x84 Ovolo Raised Panel | Thermal Sash SDL - Six Lite - Single Panel | 7' - 0" | 37526 | 2 | 1 | 1 | 7' - 2" | 3' - 2" | 2' - 10" |
| 37526 Thermal French & Sash 34x96 Ovolo Raised Panel | Thermal Sash SDL - Six Lite - Single Panel | 8' - 0" | 37526 | 2 | 1 | 1 | 8' - 2" | 3' - 2" | 2' - 10" |
| 37526 Thermal French & Sash 36x80 Ovolo Raised Panel | Thermal Sash SDL - Six Lite - Single Panel | 6' - 8" | 37526 | 2 | 1 | 1 | 6' - 10" | 3' - 4" | 3' - 0" |
| 37526 Thermal French & Sash 36x84 Ovolo Raised Panel | Thermal Sash SDL - Six Lite - Single Panel | 7' - 0" | 37526 | 2 | 1 | 1 | 7' - 2" | 3' - 4" | 3' - 0" |
| 37526 Thermal French & Sash 36x96 Ovolo Raised Panel | Thermal Sash SDL - Six Lite - Single Panel | 8' - 0" | 37526 | 2 | 1 | 1 | 8' - 2" | 3' - 4" | 3' - 0" |
| 37526 Thermal French & Sash 38x80 Ovolo Raised Panel | Thermal Sash SDL - Six Lite - Single Panel | 6' - 8" | 37526 | 2 | 1 | 1 | 6' - 10" | 3' - 6" | 3' - 2" |
| 37526 Thermal French & Sash 38x84 Ovolo Raised Panel | Thermal Sash SDL - Six Lite - Single Panel | 7' - 0" | 37526 | 2 | 1 | 1 | 7' - 2" | 3' - 6" | 3' - 2" |
| 37526 Thermal French & Sash 38x96 Ovolo Raised Panel | Thermal Sash SDL - Six Lite - Single Panel | 8' - 0" | 37526 | 2 | 1 | 1 | 8' - 2" | 3' - 6" | 3' - 2" |
| 37526 Thermal French & Sash 40x80 Ovolo Raised Panel | Thermal Sash SDL - Six Lite - Single Panel | 6' - 8" | 37526 | 2 | 1 | 1 | 6' - 10" | 3' - 8" | 3' - 4" |
| 37526 Thermal French & Sash 40x84 Ovolo Raised Panel | Thermal Sash SDL - Six Lite - Single Panel | 7' - 0" | 37526 | 2 | 1 | 1 | 7' - 2" | 3' - 8" | 3' - 4" |
| 37526 Thermal French & Sash 40x96 Ovolo Raised Panel | Thermal Sash SDL - Six Lite - Single Panel | 8' - 0" | 37526 | 2 | 1 | 1 | 8' - 2" | 3' - 8" | 3' - 4" |
| 37526 Thermal French & Sash 42x80 Ovolo Raised Panel | Thermal Sash SDL - Six Lite - Single Panel | 6' - 8" | 37526 | 2 | 1 | 1 | 6' - 10" | 3' - 10" | 3' - 6" |
| 37526 Thermal French & Sash 42x84 Ovolo Raised Panel | Thermal Sash SDL - Six Lite - Single Panel | 7' - 0" | 37526 | 2 | 1 | 1 | 7' - 2" | 3' - 10" | 3' - 6" |
| 37526 Thermal French & Sash 42x96 Ovolo Raised Panel | Thermal Sash SDL - Six Lite - Single Panel | 8' - 0" | 37526 | 2 | 1 | 1 | 8' - 2" | 3' - 10" | 3' - 6" |
| 37528 Thermal French & Sash 30x80 Ovolo Raised Panel | Thermal Sash SDL - Eight Lite - Single Panel | 6' - 8" | 37528 | 3 | 1 | 1 | 6' - 10" | 2' - 10" | 2' - 6" |
| 37528 Thermal French & Sash 30x84 Ovolo Raised Panel | Thermal Sash SDL - Eight Lite - Single Panel | 7' - 0" | 37528 | 3 | 1 | 1 | 7' - 2" | 2' - 10" | 2' - 6" |
| 37528 Thermal French & Sash 30x96 Ovolo Raised Panel | Thermal Sash SDL - Eight Lite - Single Panel | 8' - 0" | 37528 | 3 | 1 | 1 | 8' - 2" | 2' - 10" | 2' - 6" |
| 37528 Thermal French & Sash 32x80 Ovolo Raised Panel | Thermal Sash SDL - Eight Lite - Single Panel | 6' - 8" | 37528 | 3 | 1 | 1 | 6' - 10" | 3' - 0" | 2' - 8" |
| 37528 Thermal French & Sash 32x84 Ovolo Raised Panel | Thermal Sash SDL - Eight Lite - Single Panel | 7' - 0" | 37528 | 3 | 1 | 1 | 7' - 2" | 3' - 0" | 2' - 8" |
| 37528 Thermal French & Sash 32x96 Ovolo Raised Panel | Thermal Sash SDL - Eight Lite - Single Panel | 8' - 0" | 37528 | 3 | 1 | 1 | 8' - 2" | 3' - 0" | 2' - 8" |
| 37528 Thermal French & Sash 34x80 Ovolo Raised Panel | Thermal Sash SDL - Eight Lite - Single Panel | 6' - 8" | 37528 | 3 | 1 | 1 | 6' - 10" | 3' - 2" | 2' - 10" |
| 37528 Thermal French & Sash 34x84 Ovolo Raised Panel | Thermal Sash SDL - Eight Lite - Single Panel | 7' - 0" | 37528 | 3 | 1 | 1 | 7' - 2" | 3' - 2" | 2' - 10" |
| 37528 Thermal French & Sash 34x96 Ovolo Raised Panel | Thermal Sash SDL - Eight Lite - Single Panel | 8' - 0" | 37528 | 3 | 1 | 1 | 8' - 2" | 3' - 2" | 2' - 10" |
| 37528 Thermal French & Sash 36x80 Ovolo Raised Panel | Thermal Sash SDL - Eight Lite - Single Panel | 6' - 8" | 37528 | 3 | 1 | 1 | 6' - 10" | 3' - 4" | 3' - 0" |
| 37528 Thermal French & Sash 36x84 Ovolo Raised Panel | Thermal Sash SDL - Eight Lite - Single Panel | 7' - 0" | 37528 | 3 | 1 | 1 | 7' - 2" | 3' - 4" | 3' - 0" |
| 37528 Thermal French & Sash 36x96 Ovolo Raised Panel | Thermal Sash SDL - Eight Lite - Single Panel | 8' - 0" | 37528 | 3 | 1 | 1 | 8' - 2" | 3' - 4" | 3' - 0" |
| 37528 Thermal French & Sash 38x80 Ovolo Raised Panel | Thermal Sash SDL - Eight Lite - Single Panel | 6' - 8" | 37528 | 3 | 1 | 1 | 6' - 10" | 3' - 6" | 3' - 2" |
| 37528 Thermal French & Sash 38x84 Ovolo Raised Panel | Thermal Sash SDL - Eight Lite - Single Panel | 7' - 0" | 37528 | 3 | 1 | 1 | 7' - 2" | 3' - 6" | 3' - 2" |
| 37528 Thermal French & Sash 38x96 Ovolo Raised Panel | Thermal Sash SDL - Eight Lite - Single Panel | 8' - 0" | 37528 | 3 | 1 | 1 | 8' - 2" | 3' - 6" | 3' - 2" |
| 37528 Thermal French & Sash 40x80 Ovolo Raised Panel | Thermal Sash SDL - Eight Lite - Single Panel | 6' - 8" | 37528 | 3 | 1 | 1 | 6' - 10" | 3' - 8" | 3' - 4" |
| 37528 Thermal French & Sash 40x84 Ovolo Raised Panel | Thermal Sash SDL - Eight Lite - Single Panel | 7' - 0" | 37528 | 3 | 1 | 1 | 7' - 2" | 3' - 8" | 3' - 4" |
| 37528 Thermal French & Sash 40x96 Ovolo Raised Panel | Thermal Sash SDL - Eight Lite - Single Panel | 8' - 0" | 37528 | 3 | 1 | 1 | 8' - 2" | 3' - 8" | 3' - 4" |
| 37528 Thermal French & Sash 42x80 Ovolo Raised Panel | Thermal Sash SDL - Eight Lite - Single Panel | 6' - 8" | 37528 | 3 | 1 | 1 | 6' - 10" | 3' - 10" | 3' - 6" |
| 37528 Thermal French & Sash 42x84 Ovolo Raised Panel | Thermal Sash SDL - Eight Lite - Single Panel | 7' - 0" | 37528 | 3 | 1 | 1 | 7' - 2" | 3' - 10" | 3' - 6" |
| 37528 Thermal French & Sash 42x96 Ovolo Raised Panel | Thermal Sash SDL - Eight Lite - Single Panel | 8' - 0" | 37528 | 3 | 1 | 1 | 8' - 2" | 3' - 10" | 3' - 6" |

## geometry (parser evidence)
native form markers: Blend x34, Sweep x22
no freeform markers — native parametric forms only
